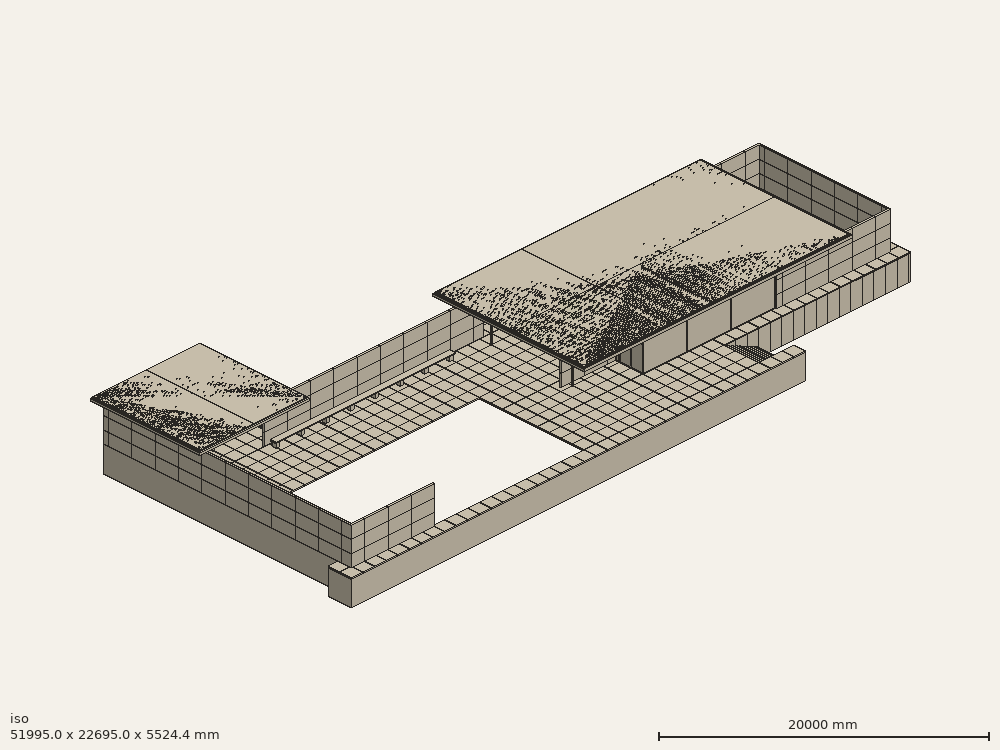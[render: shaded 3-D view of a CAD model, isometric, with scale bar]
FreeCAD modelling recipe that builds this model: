
FCSTD DOCUMENT  (FreeCAD 0.19R17174 (Git))
Label: Pabellon de Barcelona
License: All rights reserved
LicenseURL: http://en.wikipedia.org/wiki/All_rights_reserved
objects: Part::FeaturePython×94, Part::Part2DObjectPython×43, Part::Feature×31, App::DocumentObjectGroup×24, Sketcher::SketchObject×17, App::FeaturePython×11, Part::MultiCommon×6, Part::Fillet×2, TechDraw::DrawSVGTemplate×2, TechDraw::DrawPage×2, TechDraw::DrawViewDimension×2, Spreadsheet::Sheet×2, Part::Compound×1, Part::Offset2D×1, Surface::GeomFillSurface×1, Part::Cut×1, App::GeometryPython×1, TechDraw::DrawViewArch×1, TechDraw::DrawViewPart×1
note: 199 computed .brp shape members not serialized (recipe doc carries the construction recipe); baked Part::Feature solids carry a one-line shape summary decoded from their .brp

FEATURE [Part::Feature] Cancel
  Placement = pos=(-22160,-15160,0) rot=(0,0,1;0rad)
  shape: bbox 43800 x 17160 x 2e-07 mm, 0 faces, 0 solids (baked)
FEATURE [Part::Feature] Columns  label="Columns003"
  Placement = pos=(-22160,-15160,0) rot=(0,0,1;0rad)
  shape: bbox 19160 x 7160 x 2e-07 mm, 0 faces, 0 solids (baked)
FEATURE [Part::Feature] Crystal
  Placement = pos=(-22160,-15160,0) rot=(0,0,1;0rad)
  shape: bbox 43740 x 17150 x 2e-07 mm, 0 faces, 0 solids (baked)
FEATURE [Part::Feature] Doors  label="Doors003"
  Placement = pos=(-22160,-15160,0) rot=(0,0,1;0rad)
  shape: bbox 45870 x 16380 x 2e-07 mm, 0 faces, 0 solids (baked)
FEATURE [Part::Feature] Flooring  label="Flooring006"
  Placement = pos=(-22160,-15160,0) rot=(0,0,1;0rad)
  shape: bbox 52000 x 22000 x 2e-07 mm, 0 faces, 0 solids (baked)
FEATURE [Part::Feature] Furniture
  Placement = pos=(-22160,-15160,0) rot=(0,0,1;0rad)
  shape: bbox 43070 x 14280 x 2e-07 mm, 0 faces, 0 solids (baked)
FEATURE [Part::Feature] Projection
  Placement = pos=(-22160,-15160,0) rot=(0,0,1;0rad)
  shape: bbox 46650 x 18650 x 2e-07 mm, 0 faces, 0 solids (baked)
FEATURE [Part::Feature] Walls  label="Walls007"
  Placement = pos=(-22160,-15160,0) rot=(0,0,1;0rad)
  shape: bbox 50320 x 21420 x 2e-07 mm, 0 faces, 0 solids (baked)
FEATURE [App::DocumentObjectGroup] Group  label="Floor plan"
  Group = -> [Cancel,Columns,Crystal,Doors,Flooring,Furniture,Projection,Walls]
FEATURE [Part::Feature] Doors001
  Placement = pos=(-22160,-42510.2,3000) rot=(0,0,1;0rad)
  shape: bbox 618.1 x 595.2 x 2e-07 mm, 0 faces, 0 solids (baked)
FEATURE [Part::Feature] Flooring001
  Placement = pos=(-22160,-42510.2,3000) rot=(0,0,1;0rad)
  shape: bbox 52000 x 17000 x 2e-07 mm, 0 faces, 0 solids (baked)
FEATURE [Part::Feature] Furniture001
  Placement = pos=(-22160,-42510.2,3000) rot=(0,0,1;0rad)
  shape: bbox 13500 x 500 x 2e-07 mm, 0 faces, 0 solids (baked)
FEATURE [Part::Feature] Projection001
  Placement = pos=(-22160,-42510.2,3000) rot=(0,0,1;0rad)
  shape: bbox 1520 x 6220 x 2e-07 mm, 0 faces, 0 solids (baked)
FEATURE [Part::Feature] Roof
  Placement = pos=(-22160,-42510.2,3000) rot=(0,0,1;0rad)
  shape: bbox 46650 x 18650 x 2e-07 mm, 0 faces, 0 solids (baked)
FEATURE [Part::Feature] Walls001
  Placement = pos=(-22160,-42510.2,3000) rot=(0,0,1;0rad)
  shape: bbox 50320 x 15320 x 2e-07 mm, 0 faces, 0 solids (baked)
FEATURE [App::DocumentObjectGroup] Group001  label="Roof plan"
  Group = -> [Doors001,Flooring001,Furniture001,Projection001,Roof,Walls001]
FEATURE [Part::Feature] Cancel001
  Placement = pos=(-81287.8,-24500,-23959) rot=(1,0,0;1.5708rad)
  shape: bbox 11310 x 2e-07 x 2975 mm, 0 faces, 0 solids (baked)
FEATURE [Part::Feature] Columns001
  Placement = pos=(-81287.8,-24500,-23959) rot=(1,0,0;1.5708rad)
  shape: bbox 12830 x 2e-07 x 3000 mm, 0 faces, 0 solids (baked)
FEATURE [Part::Feature] Flooring002
  Placement = pos=(-81287.8,-24500,-23959) rot=(1,0,0;1.5708rad)
  shape: bbox 52000 x 2e-07 x 1600 mm, 0 faces, 0 solids (baked)
FEATURE [Part::Feature] Furniture002
  Placement = pos=(-81287.8,-24500,-23959) rot=(1,0,0;1.5708rad)
  shape: bbox 15200 x 2e-07 x 500 mm, 0 faces, 0 solids (baked)
FEATURE [Part::Feature] Roof001
  Placement = pos=(-81287.8,-24500,-23959) rot=(1,0,0;1.5708rad)
  shape: bbox 59640 x 2e-07 x 4974 mm, 0 faces, 0 solids (baked)
FEATURE [Part::Feature] Walls002
  Placement = pos=(-81287.8,-24500,-23959) rot=(1,0,0;1.5708rad)
  shape: bbox 50320 x 2e-07 x 3000 mm, 0 faces, 0 solids (baked)
FEATURE [App::DocumentObjectGroup] Group002  label="View front"
  Group = -> [Cancel001,Columns001,Flooring002,Furniture002,Roof001,Walls002]
FEATURE [Part::Feature] Cancel002
  Placement = pos=(89304.6,14800,-15495.3) rot=(0,0.707107,0.707107;3.14159rad)
  shape: bbox 32700 x 2e-07 x 3000 mm, 0 faces, 0 solids (baked)
FEATURE [Part::Feature] Columns002
  Placement = pos=(89304.6,14800,-15495.3) rot=(0,0.707107,0.707107;3.14159rad)
  shape: bbox 160 x 2e-07 x 3000 mm, 0 faces, 0 solids (baked)
FEATURE [Part::Feature] Roof002
  Placement = pos=(89304.6,14800,-15495.3) rot=(0,0.707107,0.707107;3.14159rad)
  shape: bbox 59640 x 2e-07 x 3836 mm, 0 faces, 0 solids (baked)
FEATURE [Part::Feature] Walls003
  Placement = pos=(89304.6,14800,-15495.3) rot=(0,0.707107,0.707107;3.14159rad)
  shape: bbox 50320 x 2e-07 x 3352 mm, 0 faces, 0 solids (baked)
FEATURE [App::DocumentObjectGroup] Group003  label="View back"
  Group = -> [Cancel002,Columns002,Roof002,Walls003]
FEATURE [Part::Feature] Flooring003
  Placement = pos=(-31600,63521.9,-6564.9) rot=(0.57735,-0.57735,-0.57735;2.0944rad)
  shape: bbox 2e-07 x 22160 x 3800 mm, 0 faces, 0 solids (baked)
FEATURE [Part::Feature] Roof003
  Placement = pos=(-31600,63521.9,-6564.9) rot=(0.57735,-0.57735,-0.57735;2.0944rad)
  shape: bbox 2e-07 x 18540 x 300 mm, 0 faces, 0 solids (baked)
FEATURE [Part::Feature] Walls004
  Placement = pos=(-31600,63521.9,-6564.9) rot=(0.57735,-0.57735,-0.57735;2.0944rad)
  shape: bbox 2e-07 x 26740 x 3800 mm, 0 faces, 0 solids (baked)
FEATURE [App::DocumentObjectGroup] Group004  label="View right"
  Group = -> [Flooring003,Roof003,Walls004]
FEATURE [Part::Feature] Cancel003
  Placement = pos=(39966.7,-107654,-7031.61) rot=(0.57735,0.57735,0.57735;2.0944rad)
  shape: bbox 2e-07 x 1800 x 400 mm, 0 faces, 0 solids (baked)
FEATURE [Part::Feature] Flooring004
  Placement = pos=(39966.7,-107654,-7031.61) rot=(0.57735,0.57735,0.57735;2.0944rad)
  shape: bbox 2e-07 x 6000 x 1267 mm, 0 faces, 0 solids (baked)
FEATURE [Part::Feature] Roof004
  Placement = pos=(39966.7,-107654,-7031.61) rot=(0.57735,0.57735,0.57735;2.0944rad)
  shape: bbox 2e-07 x 24790 x 4567 mm, 0 faces, 0 solids (baked)
FEATURE [Part::Feature] Walls005
  Placement = pos=(39966.7,-107654,-7031.61) rot=(0.57735,0.57735,0.57735;2.0944rad)
  shape: bbox 2e-07 x 22620 x 4267 mm, 0 faces, 0 solids (baked)
FEATURE [App::DocumentObjectGroup] Group005  label="View left"
  Group = -> [Cancel003,Flooring004,Roof004,Walls005]
FEATURE [Part::Part2DObjectPython] Wire  # Draft 2D object (typed FeaturePython)
  ChamferSize = 0
  Closed = false
  End = (-13840,840,0)
  FilletRadius = 0
  Length = 42120
  MakeFace = true
  Placement = pos=(-15000,-15160,0) rot=(0,0,1;0rad)
  Points = (5) [(0,0,0),(-7160,0,0),(-7160,21320,0),(1160,21320,0),(1160,16000,0)]
  Start = (-15000,-15160,0)
  Subdivisions = 0
FEATURE [Part::Part2DObjectPython] Line  # Draft 2D object (typed FeaturePython)
  ChamferSize = 0
  Closed = false
  End = (3330,-840,0)
  FilletRadius = 0
  Length = 18830
  MakeFace = true
  Placement = pos=(-15500,-840,0) rot=(0,0,1;0rad)
  Points = (2) [(0,0,0),(18830,0,0)]
  Start = (-15500,-840,0)
  Subdivisions = 0
FEATURE [Part::Part2DObjectPython] Wire001  # Draft 2D object (typed FeaturePython)
  ChamferSize = 0
  Closed = false
  End = (18333.3,-11160,0)
  FilletRadius = 0
  Length = 34506.7
  MakeFace = true
  Placement = pos=(14800,160,0) rot=(0,0,1;0rad)
  Points = (4) [(0,0,0),(13360,0,0),(13360,-11320,0),(3533.33,-11320,0)]
  Start = (14800,160,0)
  Subdivisions = 0
FEATURE [Part::Part2DObjectPython] Line001  # Draft 2D object (typed FeaturePython)
  ChamferSize = 0
  Closed = false
  End = (9666.67,-8670,0)
  FilletRadius = 0
  Length = 7333.33
  MakeFace = true
  Placement = pos=(2333.33,-8670,0) rot=(0,0,1;0rad)
  Points = (2) [(0,0,0),(7333.33,0,0)]
  Start = (2333.33,-8670,0)
  Subdivisions = 0
FEATURE [Part::Part2DObjectPython] Line002  # Draft 2D object (typed FeaturePython)
  ChamferSize = 0
  Closed = false
  End = (19330,-4510,0)
  FilletRadius = 0
  Length = 5160
  MakeFace = true
  Placement = pos=(14170,-4510,0) rot=(0,0,1;0rad)
  Points = (2) [(0,0,0),(5160,0,0)]
  Start = (14170,-4510,0)
  Subdivisions = 0
FEATURE [Part::Part2DObjectPython] Line003  # Draft 2D object (typed FeaturePython)
  ChamferSize = 0
  Closed = false
  End = (-18050,6000,0)
  FilletRadius = 0
  Length = 5160
  MakeFace = true
  Placement = pos=(-18050,840,0) rot=(0,0,1;0rad)
  Points = (2) [(0,0,0),(-8.73115e-11,5160,0)]
  Start = (-18050,840,0)
  Subdivisions = 0
FEATURE [Part::Part2DObjectPython] Line004  # Draft 2D object (typed FeaturePython)
  ChamferSize = 0
  Closed = false
  End = (-14000,4500,0)
  FilletRadius = 0
  Length = 3950
  MakeFace = true
  Placement = pos=(-17950,4500,0) rot=(0,0,1;0rad)
  Points = (2) [(0,0,0),(3950,0,0)]
  Start = (-17950,4500,0)
  Subdivisions = 0
FEATURE [Part::Part2DObjectPython] Line005  # Draft 2D object (typed FeaturePython)
  ChamferSize = 0
  Closed = false
  End = (-16050,4600,0)
  FilletRadius = 0
  Length = 1400
  MakeFace = true
  Placement = pos=(-16050,6000,0) rot=(0,0,1;0rad)
  Points = (2) [(0,0,0),(0,-1400,0)]
  Start = (-16050,6000,0)
  Subdivisions = 0
FEATURE [Part::FeaturePython] Wall  # Arch/BIM 150 (typed FeaturePython)
  Align = 0
  Base = -> Wire
  BlockHeight = 1000
  BlockLength = 2000
  CountBroken = 15
  CountEntire = 52
  Face = 0
  Height = 3000
  HorizontalArea = 7.3024e+06
  IfcData = IfcUID=0OLEO4RqaHwRzx093rt3ko,+1 more (map truncated)
  IfcType = 150
  Joint = 0
  Length = 42120
  MakeBlocks = true
  MoveBase = false
  MoveWithHost = true
  Normal = (0,0,0)
  OffsetFirst = 0
  OffsetSecond = 0
  PerimeterLength = 83600
  PredefinedType = 0
  VerticalArea = 2.46192e+08
  Width = 160
FEATURE [Part::FeaturePython] Wall001  # Arch/BIM 150 (typed FeaturePython)
  Align = 0
  Base = -> Line
  BlockHeight = 1000
  BlockLength = 2000
  CountBroken = 3
  CountEntire = 27
  Face = 0
  Height = 3000
  HorizontalArea = 3.0128e+06
  IfcData = IfcUID=0OKnYcRqaHwRzx093rt3ko,+1 more (map truncated)
  IfcType = 150
  Joint = 0
  Length = 18830
  MakeBlocks = true
  MoveBase = false
  MoveWithHost = true
  Normal = (0,0,0)
  OffsetFirst = 0
  OffsetSecond = 0
  PerimeterLength = 37980
  PredefinedType = 0
  VerticalArea = 1.1394e+08
  Width = 160
FEATURE [Part::FeaturePython] Wall002  # Arch/BIM 150 (typed FeaturePython)
  Align = 0
  Base = -> Wire001
  BlockHeight = 1000
  BlockLength = 2000
  CountBroken = 9
  CountEntire = 45
  Face = 0
  Height = 3000
  HorizontalArea = 5.46987e+06
  IfcData = IfcUID=0ONTaSRqaHwRzx093rt3ko,+1 more (map truncated)
  IfcType = 150
  Joint = 0
  Length = 34506.7
  MakeBlocks = true
  MoveBase = false
  MoveWithHost = true
  Normal = (0,0,0)
  OffsetFirst = 0
  OffsetSecond = 0
  PerimeterLength = 68693.3
  PredefinedType = 0
  VerticalArea = 2.0608e+08
  Width = 160
FEATURE [Part::FeaturePython] Wall003  # Arch/BIM 150 (typed FeaturePython)
  Align = 1
  Base = -> Line001
  BlockHeight = 1000
  BlockLength = 2000
  CountBroken = 3
  CountEntire = 9
  Face = 0
  Height = 3000
  HorizontalArea = 1.17333e+06
  IfcData = IfcUID=0OO35ERqaHwRzx093rt3ko,+1 more (map truncated)
  IfcType = 150
  Joint = 0
  Length = 7333.33
  MakeBlocks = true
  MoveBase = false
  MoveWithHost = true
  Normal = (0,0,0)
  OffsetFirst = 0
  OffsetSecond = 0
  PerimeterLength = 14986.7
  PredefinedType = 0
  VerticalArea = 4.496e+07
  Width = 160
FEATURE [Part::FeaturePython] Wall004  # Arch/BIM 150 (typed FeaturePython)
  Align = 0
  Base = -> Line002
  BlockHeight = 0
  BlockLength = 0
  CountBroken = 0
  CountEntire = 0
  Face = 0
  Height = 3000
  HorizontalArea = 825600
  IfcData = IfcUID=0OORcIRqaHwRzx093rt3ko,+1 more (map truncated)
  IfcType = 150
  Joint = 0
  Length = 5160
  MakeBlocks = false
  MoveBase = false
  MoveWithHost = true
  Normal = (0,0,0)
  OffsetFirst = 0
  OffsetSecond = 0
  PerimeterLength = 10640
  PredefinedType = 0
  VerticalArea = 3.192e+07
  Width = 160
FEATURE [Part::FeaturePython] Wall005  # Arch/BIM 150 (typed FeaturePython)
  Align = 0
  Base = -> Line003
  BlockHeight = 0
  BlockLength = 0
  CountBroken = 0
  CountEntire = 0
  Face = 0
  Height = 3000
  HorizontalArea = 516000
  IfcData = IfcUID=0OOnwaRqaHwRzx093rt3ko,+1 more (map truncated)
  IfcType = 150
  Joint = 0
  Length = 5160
  MakeBlocks = false
  MoveBase = false
  MoveWithHost = true
  Normal = (0,0,0)
  OffsetFirst = 0
  OffsetSecond = 0
  PerimeterLength = 10520
  PredefinedType = 0
  VerticalArea = 2.778e+07
  Width = 100
FEATURE [Part::FeaturePython] Wall006  # Arch/BIM 150 (typed FeaturePython)
  Align = 1
  Base = -> Line004
  BlockHeight = 0
  BlockLength = 0
  CountBroken = 0
  CountEntire = 0
  Face = 0
  Height = 3000
  HorizontalArea = 395000
  IfcData = IfcUID=0OQ8YARqaHwRzx093rt3ko,+1 more (map truncated)
  IfcType = 150
  Joint = 0
  Length = 3950
  MakeBlocks = false
  MoveBase = false
  MoveWithHost = true
  Normal = (0,0,0)
  OffsetFirst = 0
  OffsetSecond = 0
  PerimeterLength = 8100
  PredefinedType = 0
  VerticalArea = 2.136e+07
  Width = 100
FEATURE [Part::FeaturePython] Wall007  # Arch/BIM 150 (typed FeaturePython)
  Align = 1
  Base = -> Line005
  BlockHeight = 0
  BlockLength = 0
  CountBroken = 0
  CountEntire = 0
  Face = 0
  Height = 3000
  HorizontalArea = 140000
  IfcData = IfcUID=0ORbNGRqaHwRzx093rt3ko,+1 more (map truncated)
  IfcType = 150
  Joint = 0
  Length = 1400
  MakeBlocks = false
  MoveBase = false
  MoveWithHost = true
  Normal = (0,0,0)
  OffsetFirst = 0
  OffsetSecond = 0
  PerimeterLength = 3000
  PredefinedType = 0
  VerticalArea = 5640000
  Width = 100
FEATURE [Part::Part2DObjectPython] Rectangle  # Draft 2D object (typed FeaturePython)
  ChamferSize = 0
  Columns = 1
  FilletRadius = 0
  Height = 600
  Length = 4000
  MakeFace = false
  Placement = pos=(-14000,6160,2000) rot=(0,0.707107,0.707107;3.14159rad)
  Rows = 1
  Support = -> [Wall]
FEATURE [Part::Part2DObjectPython] Rectangle001  # Draft 2D object (typed FeaturePython)
  ChamferSize = 0
  Columns = 1
  FilletRadius = 0
  Height = 400
  Length = 1850
  MakeFace = false
  Placement = pos=(-14100,6160,2100) rot=(0,0.707107,0.707107;3.14159rad)
  Rows = 1
FEATURE [Part::Part2DObjectPython] Rectangle002  # Draft 2D object (typed FeaturePython)
  ChamferSize = 0
  Columns = 1
  FilletRadius = 0
  Height = 400
  Length = 1850
  MakeFace = false
  Placement = pos=(-16050,6160,2100) rot=(0,0.707107,0.707107;3.14159rad)
  Rows = 1
FEATURE [Part::Compound] Compound
  Links = -> [Rectangle,Rectangle001,Rectangle002]
FEATURE [Part::FeaturePython] Window  # Arch/BIM 154 (typed FeaturePython)
  Area = 0
  Base = -> Compound
  Frame = 0
  Height = 0
  HoleDepth = 0
  HoleWire = 0
  HorizontalArea = 0
  Hosts = -> [Wall]
  IfcData = IfcUID=0OMAYERqaHwRzx093rt3ko,+1 more (map truncated)
  IfcType = 154
  LouvreSpacing = 0
  LouvreWidth = 0
  MoveBase = false
  MoveWithHost = true
  Normal = (0,-1,0)
  Offset = 55
  Opening = 0
  OverallHeight = 0
  OverallWidth = 0
  PartitioningType = 0
  PerimeterLength = 0
  PredefinedType = 0
  Preset = 0
  SymbolElevation = false
  SymbolPlan = false
  VerticalArea = 0
  Width = 0
  WindowParts = Window frame | Frame | Wire0,Wire1,Wire2 | 50.0 | 0.0+V | Glass 1 | Glass panel | Wire1 | 10.0 | 20.0+V | Glass 2 | Glass panel | Wire2 | 10.0 | 20.0+V
  expr: OverallWidth = Width.Value
  expr: OverallHeight = Height.Value
FEATURE [Sketcher::SketchObject] Sketch
  Placement = pos=(-17150,4500,0) rot=(1,0,0;1.5708rad)
  sketch-geometry (8):
    g0: LineSegment StartX=0 StartY=0 StartZ=0 EndX=800 EndY=0 EndZ=0
    g1: LineSegment StartX=800 StartY=0 StartZ=0 EndX=800 EndY=2100 EndZ=0
    g2: LineSegment StartX=800 StartY=2100 StartZ=0 EndX=0 EndY=2100 EndZ=0
    g3: LineSegment StartX=0 StartY=2100 StartZ=0 EndX=0 EndY=0 EndZ=0
    g4: LineSegment StartX=30 StartY=0 StartZ=0 EndX=770 EndY=0 EndZ=0
    g5: LineSegment StartX=770 StartY=0 StartZ=0 EndX=770 EndY=2070 EndZ=0
    g6: LineSegment StartX=770 StartY=2070 StartZ=0 EndX=30 EndY=2070 EndZ=0
    g7: LineSegment StartX=30 StartY=2070 StartZ=0 EndX=30 EndY=0 EndZ=0
  constraints (23):
    c: Coincident(g0,g1)
    c: Coincident(g1,g2)
    c: Coincident(g2,g3)
    c: Coincident(g3,g0)
    c: Horizontal(g0)
    c: Horizontal(g2)
    c: Vertical(g1)
    c: Vertical(g3)
    c: Coincident(g4,g5)
    c: Coincident(g5,g6)
    c: Coincident(g6,g7)
    c: Coincident(g7,g4)
    c: Horizontal(g4)
    c: Horizontal(g6)
    c: Vertical(g5)
    c: Vertical(g7)
    c: DistanceY(g1) = 2100  'Height'
    c: DistanceX(g0) = 800  'Width'
    c: DistanceY(g6,g2) = 30  'Frame1'
    c: DistanceX(g2,g6) = 30  'Frame2'
    c: DistanceX(g4,g0) = 30  'Frame3'
    c: DistanceY(g0,g4) = 0
    c: Coincident(g0,g-1)
FEATURE [Part::FeaturePython] Window001  label="Wooden door 80x210 001"  # Arch/BIM 41 (typed FeaturePython)
  Area = 1680000
  Base = -> Sketch
  Frame = 30
  Height = 2100
  HoleDepth = 0
  HoleWire = 0
  HorizontalArea = 0
  Hosts = -> [Wall006]
  IfcData = IfcUID=0OQpl0RqaHwRzx093rt3ko,+1 more (map truncated)
  IfcType = 41
  LouvreSpacing = 0
  LouvreWidth = 0
  MoveBase = false
  MoveWithHost = true
  Normal = (0,1,-2e-16)
  Opening = 0
  OperationType = 0
  OverallHeight = 2100
  OverallWidth = 800
  PerimeterLength = 0
  PredefinedType = 0
  Preset = 6
  SymbolElevation = false
  SymbolPlan = false
  VerticalArea = 0
  Width = 800
  WindowParts = OuterFrame | Frame | Wire0,Wire1 | 30.0+V | 0.00+V | Door | Solid panel | Wire1 | 30.0 | 30.0+V
  expr: OverallWidth = Width.Value
  expr: OverallHeight = Height.Value
FEATURE [Sketcher::SketchObject] Sketch001
  Placement = pos=(-16050,5400,0) rot=(0.57735,-0.57735,-0.57735;2.0944rad)
  sketch-geometry (8):
    g0: LineSegment StartX=0 StartY=0 StartZ=0 EndX=800 EndY=0 EndZ=0
    g1: LineSegment StartX=800 StartY=0 StartZ=0 EndX=800 EndY=2100 EndZ=0
    g2: LineSegment StartX=800 StartY=2100 StartZ=0 EndX=0 EndY=2100 EndZ=0
    g3: LineSegment StartX=0 StartY=2100 StartZ=0 EndX=0 EndY=0 EndZ=0
    g4: LineSegment StartX=30 StartY=0 StartZ=0 EndX=770 EndY=0 EndZ=0
    g5: LineSegment StartX=770 StartY=0 StartZ=0 EndX=770 EndY=2070 EndZ=0
    g6: LineSegment StartX=770 StartY=2070 StartZ=0 EndX=30 EndY=2070 EndZ=0
    g7: LineSegment StartX=30 StartY=2070 StartZ=0 EndX=30 EndY=0 EndZ=0
  constraints (23):
    c: Coincident(g0,g1)
    c: Coincident(g1,g2)
    c: Coincident(g2,g3)
    c: Coincident(g3,g0)
    c: Horizontal(g0)
    c: Horizontal(g2)
    c: Vertical(g1)
    c: Vertical(g3)
    c: Coincident(g4,g5)
    c: Coincident(g5,g6)
    c: Coincident(g6,g7)
    c: Coincident(g7,g4)
    c: Horizontal(g4)
    c: Horizontal(g6)
    c: Vertical(g5)
    c: Vertical(g7)
    c: DistanceY(g1) = 2100  'Height'
    c: DistanceX(g0) = 800  'Width'
    c: DistanceY(g6,g2) = 30  'Frame1'
    c: DistanceX(g2,g6) = 30  'Frame2'
    c: DistanceX(g4,g0) = 30  'Frame3'
    c: DistanceY(g0,g4) = 0
    c: Coincident(g0,g-1)
FEATURE [Part::FeaturePython] Window002  label="Wooden door 80x210 "  # Arch/BIM 41 (typed FeaturePython)
  Area = 1680000
  Base = -> Sketch001
  Frame = 30
  Height = 2100
  HoleDepth = 0
  HoleWire = 0
  HorizontalArea = 0
  Hosts = -> [Wall007]
  IfcData = IfcUID=0OSF62RqaHwRzx093rt3ko,+1 more (map truncated)
  IfcType = 41
  LouvreSpacing = 0
  LouvreWidth = 0
  MoveBase = false
  MoveWithHost = true
  Normal = (1,0,0)
  Opening = 0
  OperationType = 0
  OverallHeight = 2100
  OverallWidth = 800
  PerimeterLength = 0
  PredefinedType = 0
  Preset = 6
  SymbolElevation = false
  SymbolPlan = false
  VerticalArea = 0
  Width = 800
  WindowParts = OuterFrame | Frame | Wire0,Wire1 | 30.0+V | 0.00+V | Door | Solid panel | Wire1 | 30.0 | 30.0+V
  expr: OverallWidth = Width.Value
  expr: OverallHeight = Height.Value
FEATURE [Sketcher::SketchObject] Sketch002
  Placement = pos=(-17950,3000,0) rot=(0.57735,0.57735,0.57735;2.0944rad)
  sketch-geometry (8):
    g0: LineSegment StartX=0 StartY=0 StartZ=0 EndX=1000 EndY=0 EndZ=0
    g1: LineSegment StartX=1000 StartY=0 StartZ=0 EndX=1000 EndY=2100 EndZ=0
    g2: LineSegment StartX=1000 StartY=2100 StartZ=0 EndX=0 EndY=2100 EndZ=0
    g3: LineSegment StartX=0 StartY=2100 StartZ=0 EndX=0 EndY=0 EndZ=0
    g4: LineSegment StartX=30 StartY=0 StartZ=0 EndX=970 EndY=0 EndZ=0
    g5: LineSegment StartX=970 StartY=0 StartZ=0 EndX=970 EndY=2070 EndZ=0
    g6: LineSegment StartX=970 StartY=2070 StartZ=0 EndX=30 EndY=2070 EndZ=0
    g7: LineSegment StartX=30 StartY=2070 StartZ=0 EndX=30 EndY=0 EndZ=0
  constraints (23):
    c: Coincident(g0,g1)
    c: Coincident(g1,g2)
    c: Coincident(g2,g3)
    c: Coincident(g3,g0)
    c: Horizontal(g0)
    c: Horizontal(g2)
    c: Vertical(g1)
    c: Vertical(g3)
    c: Coincident(g4,g5)
    c: Coincident(g5,g6)
    c: Coincident(g6,g7)
    c: Coincident(g7,g4)
    c: Horizontal(g4)
    c: Horizontal(g6)
    c: Vertical(g5)
    c: Vertical(g7)
    c: DistanceY(g1) = 2100  'Height'
    c: DistanceX(g0) = 1000  'Width'
    c: DistanceY(g6,g2) = 30  'Frame1'
    c: DistanceX(g2,g6) = 30  'Frame2'
    c: DistanceX(g4,g0) = 30  'Frame3'
    c: DistanceY(g0,g4) = 0
    c: Coincident(g0,g-1)
FEATURE [Part::FeaturePython] Window003  label="Wooden door 100x210"  # Arch/BIM 41 (typed FeaturePython)
  Area = 2100000
  Base = -> Sketch002
  Frame = 30
  Height = 2100
  HoleDepth = 0
  HoleWire = 0
  HorizontalArea = 0
  Hosts = -> [Wall005]
  IfcData = IfcUID=0OPMYARqaHwRzx093rt3ko,+1 more (map truncated)
  IfcType = 41
  LouvreSpacing = 0
  LouvreWidth = 0
  MoveBase = false
  MoveWithHost = true
  Normal = (-1,-8.4e-15,8.4e-15)
  Opening = 0
  OperationType = 0
  OverallHeight = 2100
  OverallWidth = 1000
  PerimeterLength = 0
  PredefinedType = 0
  Preset = 6
  SymbolElevation = false
  SymbolPlan = false
  VerticalArea = 0
  Width = 1000
  WindowParts = OuterFrame | Frame | Wire0,Wire1 | 30.0+V | 0.00+V | Door | Solid panel | Wire1 | 30.0 | 30.0+V
  expr: OverallWidth = Width.Value
  expr: OverallHeight = Height.Value
FEATURE [Sketcher::SketchObject] Sketch003
  Placement = pos=(4800,-11100,0) rot=(1,0,0;1.5708rad)
  sketch-geometry (24):
    g0: LineSegment StartX=0 StartY=0 StartZ=0 EndX=2000 EndY=0 EndZ=0
    g1: LineSegment StartX=2000 StartY=0 StartZ=0 EndX=2000 EndY=2100 EndZ=0
    g2: LineSegment StartX=2000 StartY=2100 StartZ=0 EndX=0 EndY=2100 EndZ=0
    g3: LineSegment StartX=0 StartY=2100 StartZ=0 EndX=0 EndY=0 EndZ=0
    g4: LineSegment StartX=30 StartY=1.7147 StartZ=0 EndX=1970 EndY=1.7147 EndZ=0
    g5: LineSegment StartX=1970 StartY=1.7147 StartZ=0 EndX=1970 EndY=2070 EndZ=0
    g6: LineSegment StartX=1970 StartY=2070 StartZ=0 EndX=30 EndY=2070 EndZ=0
    g7: LineSegment StartX=30 StartY=2070 StartZ=0 EndX=30 EndY=1.7147 EndZ=0
    g8: LineSegment StartX=33 StartY=4.7147 StartZ=0 EndX=998.5 EndY=4.7147 EndZ=0
    g9: LineSegment StartX=998.5 StartY=4.7147 StartZ=0 EndX=998.5 EndY=2067 EndZ=0
    g10: LineSegment StartX=998.5 StartY=2067 StartZ=0 EndX=33 EndY=2067 EndZ=0
    g11: LineSegment StartX=33 StartY=2067 StartZ=0 EndX=33 EndY=4.7147 EndZ=0
    g12: LineSegment StartX=63 StartY=34.7147 StartZ=0 EndX=968.5 EndY=34.7147 EndZ=0
    g13: LineSegment StartX=968.5 StartY=34.7147 StartZ=0 EndX=968.5 EndY=2037 EndZ=0
    g14: LineSegment StartX=968.5 StartY=2037 StartZ=0 EndX=63 EndY=2037 EndZ=0
    g15: LineSegment StartX=63 StartY=2037 StartZ=0 EndX=63 EndY=34.7147 EndZ=0
    g16: LineSegment StartX=1001.5 StartY=4.7147 StartZ=0 EndX=1967 EndY=4.7147 EndZ=0
    g17: LineSegment StartX=1967 StartY=4.7147 StartZ=0 EndX=1967 EndY=2067 EndZ=0
    g18: LineSegment StartX=1967 StartY=2067 StartZ=0 EndX=1001.5 EndY=2067 EndZ=0
    g19: LineSegment StartX=1001.5 StartY=2067 StartZ=0 EndX=1001.5 EndY=4.7147 EndZ=0
    g20: LineSegment StartX=1031.5 StartY=34.7147 StartZ=0 EndX=1937 EndY=34.7147 EndZ=0
    g21: LineSegment StartX=1937 StartY=34.7147 StartZ=0 EndX=1937 EndY=2037 EndZ=0
    g22: LineSegment StartX=1937 StartY=2037 StartZ=0 EndX=1031.5 EndY=2037 EndZ=0
    g23: LineSegment StartX=1031.5 StartY=2037 StartZ=0 EndX=1031.5 EndY=34.7147 EndZ=0
  constraints (70):
    c: Coincident(g0,g1)
    c: Coincident(g1,g2)
    c: Coincident(g2,g3)
    c: Coincident(g3,g0)
    c: Horizontal(g0)
    c: Horizontal(g2)
    c: Vertical(g1)
    c: Vertical(g3)
    c: Coincident(g4,g5)
    c: Coincident(g5,g6)
    c: Coincident(g6,g7)
    c: Coincident(g7,g4)
    c: Horizontal(g4)
    c: Horizontal(g6)
    c: Vertical(g5)
    c: Vertical(g7)
    c: DistanceY(g1) = 2100  'Height'
    c: DistanceX(g0) = 2000  'Width'
    c: DistanceY(g6,g2) = 30  'Frame1'
    c: DistanceX(g2,g6) = 30  'Frame2'
    c: DistanceX(g4,g0) = 30  'Frame3'
    c: Coincident(g0,g-1)
    c: Coincident(g8,g9)
    c: Coincident(g9,g10)
    c: Coincident(g10,g11)
    c: Coincident(g11,g8)
    c: Horizontal(g8)
    c: Horizontal(g10)
    c: Vertical(g9)
    c: Vertical(g11)
    c: Coincident(g12,g13)
    c: Coincident(g13,g14)
    c: Coincident(g14,g15)
    c: Coincident(g15,g12)
    c: Horizontal(g12)
    c: Horizontal(g14)
    c: Vertical(g13)
    c: Vertical(g15)
    c: Coincident(g16,g17)
    c: Coincident(g17,g18)
    c: Coincident(g18,g19)
    c: Coincident(g19,g16)
    c: Horizontal(g16)
    c: Horizontal(g18)
    c: Vertical(g17)
    c: Vertical(g19)
    c: Coincident(g20,g21)
    c: Coincident(g21,g22)
    c: Coincident(g22,g23)
    c: Coincident(g23,g20)
    c: Horizontal(g20)
    c: Horizontal(g22)
    c: Vertical(g21)
    c: Vertical(g23)
    c: DistanceY(g8,g12) = 30  'Frame5'
    c: DistanceX(g8,g12) = 30  'Frame6'
    c: DistanceX(g21,g17) = 30  'Frame7'
    c: DistanceY(g21,g17) = 30  'Frame8'
    c: DistanceX(g16,g20) = 30  'Frame9'
    c: DistanceX(g14,g10) = 30  'Frame10'
    c: Equal(g22,g14)
    c: DistanceY(g8,g16) = 0
    c: DistanceY(g10,g18) = 0
    c: DistanceX(g4,g8) = 3
    c: DistanceY(g4,g8) = 3
    c: DistanceX(g6,g18) = -3
    c: DistanceY(g6,g18) = -3
    c: DistanceX(g9,g19) = 3
    c: PointOnObject(g13,g22)
    c: PointOnObject(g20,g12)
FEATURE [Part::FeaturePython] Window004  label="Glass door double 200x210 "  # Arch/BIM 41 (typed FeaturePython)
  Area = 4200000
  Base = -> Sketch003
  Frame = 30
  Height = 2100
  HoleDepth = 0
  HoleWire = 0
  HorizontalArea = 0
  IfcData = IfcUID=0OgMsCRqaHwRzx093rt3ko,+1 more (map truncated)
  IfcType = 41
  LouvreSpacing = 0
  LouvreWidth = 0
  MoveBase = false
  MoveWithHost = true
  Normal = (0,1,-2e-16)
  Opening = 0
  OperationType = 0
  OverallHeight = 2100
  OverallWidth = 2000
  PerimeterLength = 0
  Placement = pos=(18100,-4200,0) rot=(0,0,-1;1.5708rad)
  PredefinedType = 0
  Preset = 3
  SymbolElevation = false
  SymbolPlan = false
  VerticalArea = 0
  Width = 2000
  WindowParts = OuterFrame | Frame | Wire0,Wire1 | 30.0+V | 0.00+V | LeftFrame | Frame | Wire2,Wire3 | 30.0 | 30.0+V | LeftGlass | Glass panel | Wire3 | 3.0 | 45.0+V | RightFrame | Frame | Wire4,Wire5 | 30.0 | 30.0+V | RightGlass | Glass panel | Wire5 | 3.0 | 45.0+V
  expr: OverallWidth = Width.Value
  expr: OverallHeight = Height.Value
FEATURE [Part::FeaturePython] Window005  label="Glass door double 200x210 001"  # Arch/BIM 41 (typed FeaturePython)
  Area = 4200000
  CloneOf = -> Window004
  Frame = 0
  Height = 2100
  HoleDepth = 0
  HoleWire = 0
  HorizontalArea = 0
  IfcData = IfcUID=0OiBIsRqaHwRzx093rt3ko,+1 more (map truncated)
  IfcType = 41
  LouvreSpacing = 0
  LouvreWidth = 0
  MoveBase = false
  MoveWithHost = true
  Normal = (0,0,0)
  Opening = 0
  OperationType = 0
  OverallHeight = 2100
  OverallWidth = 2000
  PerimeterLength = 0
  Placement = pos=(27070,4800,0) rot=(0,0,-1;1.5708rad)
  PredefinedType = 0
  Preset = 0
  SymbolElevation = false
  SymbolPlan = false
  VerticalArea = 0
  Width = 2000
  expr: OverallWidth = Width.Value
  expr: OverallHeight = Height.Value
FEATURE [Sketcher::SketchObject] Sketch004
  Placement = pos=(-15975,974.662,0) rot=(1,0,0;1.5708rad)
  sketch-geometry (16):
    g0: LineSegment StartX=0 StartY=0 StartZ=0 EndX=950 EndY=0 EndZ=0
    g1: LineSegment StartX=950 StartY=0 StartZ=0 EndX=950 EndY=2100 EndZ=0
    g2: LineSegment StartX=950 StartY=2100 StartZ=0 EndX=0 EndY=2100 EndZ=0
    g3: LineSegment StartX=0 StartY=2100 StartZ=0 EndX=0 EndY=0 EndZ=0
    g4: LineSegment StartX=30 StartY=0 StartZ=0 EndX=920 EndY=0 EndZ=0
    g5: LineSegment StartX=920 StartY=0 StartZ=0 EndX=920 EndY=2070 EndZ=0
    g6: LineSegment StartX=920 StartY=2070 StartZ=0 EndX=30 EndY=2070 EndZ=0
    g7: LineSegment StartX=30 StartY=2070 StartZ=0 EndX=30 EndY=0 EndZ=0
    g8: LineSegment StartX=33 StartY=3 StartZ=0 EndX=917 EndY=3 EndZ=0
    g9: LineSegment StartX=917 StartY=3 StartZ=0 EndX=917 EndY=2067 EndZ=0
    g10: LineSegment StartX=917 StartY=2067 StartZ=0 EndX=33 EndY=2067 EndZ=0
    g11: LineSegment StartX=33 StartY=2067 StartZ=0 EndX=33 EndY=3 EndZ=0
    g12: LineSegment StartX=63 StartY=33 StartZ=0 EndX=887 EndY=33 EndZ=0
    g13: LineSegment StartX=887 StartY=33 StartZ=0 EndX=887 EndY=2037 EndZ=0
    g14: LineSegment StartX=887 StartY=2037 StartZ=0 EndX=63 EndY=2037 EndZ=0
    g15: LineSegment StartX=63 StartY=2037 StartZ=0 EndX=63 EndY=33 EndZ=0
  constraints (47):
    c: Coincident(g0,g1)
    c: Coincident(g1,g2)
    c: Coincident(g2,g3)
    c: Coincident(g3,g0)
    c: Horizontal(g0)
    c: Horizontal(g2)
    c: Vertical(g1)
    c: Vertical(g3)
    c: Coincident(g4,g5)
    c: Coincident(g5,g6)
    c: Coincident(g6,g7)
    c: Coincident(g7,g4)
    c: Horizontal(g4)
    c: Horizontal(g6)
    c: Vertical(g5)
    c: Vertical(g7)
    c: DistanceY(g1) = 2100  'Height'
    c: DistanceX(g0) = 950  'Width'
    c: DistanceY(g6,g2) = 30  'Frame1'
    c: DistanceX(g2,g6) = 30  'Frame2'
    c: DistanceX(g4,g0) = 30  'Frame3'
    c: DistanceY(g0,g4) = 0
    c: Coincident(g0,g-1)
    c: Coincident(g8,g9)
    c: Coincident(g9,g10)
    c: Coincident(g10,g11)
    c: Coincident(g11,g8)
    c: Horizontal(g8)
    c: Horizontal(g10)
    c: Vertical(g9)
    c: Vertical(g11)
    c: Coincident(g12,g13)
    c: Coincident(g13,g14)
    c: Coincident(g14,g15)
    c: Coincident(g15,g12)
    c: Horizontal(g12)
    c: Horizontal(g14)
    c: Vertical(g13)
    c: Vertical(g15)
    c: DistanceX(g8,g12) = 30  'Frame5'
    c: DistanceY(g8,g12) = 30  'Frame6'
    c: DistanceX(g14,g10) = 30  'Frame8'
    c: DistanceY(g14,g10) = 30  'Frame7'
    c: DistanceX(g4,g8) = 3
    c: DistanceY(g4,g8) = 3
    c: DistanceX(g10,g6) = 3
    c: DistanceY(g10,g6) = 3
FEATURE [Part::FeaturePython] Window006  label="Glass door simple 95x210"  # Arch/BIM 41 (typed FeaturePython)
  Area = 1995000
  Base = -> Sketch004
  Frame = 30
  Height = 2100
  HoleDepth = 0
  HoleWire = 0
  HorizontalArea = 0
  IfcData = IfcUID=0OiKJuRqaHwRzx093rt3ko,+1 more (map truncated)
  IfcType = 41
  LouvreSpacing = 0
  LouvreWidth = 0
  MoveBase = false
  MoveWithHost = true
  Normal = (0,1,-2e-16)
  Opening = 0
  OperationType = 0
  OverallHeight = 2100
  OverallWidth = 950
  PerimeterLength = 0
  PredefinedType = 0
  Preset = 7
  SymbolElevation = false
  SymbolPlan = false
  VerticalArea = 0
  Width = 950
  WindowParts = OuterFrame | Frame | Wire0,Wire1 | 30.0+V | 0.00+V | InnerFrame | Frame | Wire2,Wire3 | 30.0 | 30.0+V | InnerGlass | Glass panel | Wire3 | 3.0 | 45.0+V
  expr: OverallWidth = Width.Value
  expr: OverallHeight = Height.Value
FEATURE [Sketcher::SketchObject] Sketch005
  Placement = pos=(-20400,-1800,0) rot=(0.57735,0.57735,0.57735;2.0944rad)
  sketch-geometry (8):
    g0: LineSegment StartX=0 StartY=0 StartZ=0 EndX=2000 EndY=0 EndZ=0
    g1: LineSegment StartX=2000 StartY=0 StartZ=0 EndX=2000 EndY=3000 EndZ=0
    g2: LineSegment StartX=2000 StartY=3000 StartZ=0 EndX=0 EndY=3000 EndZ=0
    g3: LineSegment StartX=0 StartY=3000 StartZ=0 EndX=0 EndY=0 EndZ=0
    g4: LineSegment StartX=20 StartY=20 StartZ=0 EndX=1980 EndY=20 EndZ=0
    g5: LineSegment StartX=1980 StartY=20 StartZ=0 EndX=1980 EndY=2980 EndZ=0
    g6: LineSegment StartX=1980 StartY=2980 StartZ=0 EndX=20 EndY=2980 EndZ=0
    g7: LineSegment StartX=20 StartY=2980 StartZ=0 EndX=20 EndY=20 EndZ=0
  constraints (23):
    c: Coincident(g0,g1)
    c: Coincident(g1,g2)
    c: Coincident(g2,g3)
    c: Coincident(g3,g0)
    c: Horizontal(g0)
    c: Horizontal(g2)
    c: Vertical(g1)
    c: Vertical(g3)
    c: Coincident(g4,g5)
    c: Coincident(g5,g6)
    c: Coincident(g6,g7)
    c: Coincident(g7,g4)
    c: Horizontal(g4)
    c: Horizontal(g6)
    c: Vertical(g5)
    c: Vertical(g7)
    c: DistanceY(g1) = 3000  'Height'
    c: DistanceX(g0) = 2000  'Width'
    c: DistanceY(g6,g2) = 20  'Frame1'
    c: DistanceX(g2,g6) = 20  'Frame2'
    c: DistanceX(g4,g0) = 20  'Frame3'
    c: DistanceY(g0,g4) = 20  'Frame4'
    c: Coincident(g0,g-1)
FEATURE [Part::FeaturePython] Window007  label="Window 200x300"  # Arch/BIM 154 (typed FeaturePython)
  Area = 6000000
  Base = -> Sketch005
  Frame = 20
  Height = 3000
  HoleDepth = 0
  HoleWire = 0
  HorizontalArea = 0
  IfcData = IfcUID=0ObaA4RqaHwRzx093rt3ko,+1 more (map truncated)
  IfcType = 154
  LouvreSpacing = 0
  LouvreWidth = 0
  MoveBase = false
  MoveWithHost = true
  Normal = (-1,0,0)
  Opening = 0
  OverallHeight = 3000
  OverallWidth = 2000
  PartitioningType = 0
  PerimeterLength = 0
  Placement = pos=(-20200,-19425.3,0) rot=(0,0,-1;1.5708rad)
  PredefinedType = 0
  Preset = 1
  SymbolElevation = false
  SymbolPlan = false
  VerticalArea = 0
  Width = 2000
  WindowParts = OuterFrame | Frame | Wire0,Wire1 | 30.0+V | 0.0+V | Glass | Glass panel | Wire1 | 2.0 | 10.0+V
  expr: OverallWidth = Width.Value
  expr: OverallHeight = Height.Value
FEATURE [Sketcher::SketchObject] Sketch006
  Placement = pos=(-18700,-900,0) rot=(1,0,0;1.5708rad)
  sketch-geometry (8):
    g0: LineSegment StartX=0 StartY=0 StartZ=0 EndX=1950 EndY=0 EndZ=0
    g1: LineSegment StartX=1950 StartY=0 StartZ=0 EndX=1950 EndY=3000 EndZ=0
    g2: LineSegment StartX=1950 StartY=3000 StartZ=0 EndX=0 EndY=3000 EndZ=0
    g3: LineSegment StartX=0 StartY=3000 StartZ=0 EndX=0 EndY=0 EndZ=0
    g4: LineSegment StartX=20 StartY=20 StartZ=0 EndX=1930 EndY=20 EndZ=0
    g5: LineSegment StartX=1930 StartY=20 StartZ=0 EndX=1930 EndY=2980 EndZ=0
    g6: LineSegment StartX=1930 StartY=2980 StartZ=0 EndX=20 EndY=2980 EndZ=0
    g7: LineSegment StartX=20 StartY=2980 StartZ=0 EndX=20 EndY=20 EndZ=0
  constraints (23):
    c: Coincident(g0,g1)
    c: Coincident(g1,g2)
    c: Coincident(g2,g3)
    c: Coincident(g3,g0)
    c: Horizontal(g0)
    c: Horizontal(g2)
    c: Vertical(g1)
    c: Vertical(g3)
    c: Coincident(g4,g5)
    c: Coincident(g5,g6)
    c: Coincident(g6,g7)
    c: Coincident(g7,g4)
    c: Horizontal(g4)
    c: Horizontal(g6)
    c: Vertical(g5)
    c: Vertical(g7)
    c: DistanceY(g1) = 3000  'Height'
    c: DistanceX(g0) = 1950  'Width'
    c: DistanceY(g6,g2) = 20  'Frame1'
    c: DistanceX(g2,g6) = 20  'Frame2'
    c: DistanceX(g4,g0) = 20  'Frame3'
    c: DistanceY(g0,g4) = 20  'Frame4'
    c: Coincident(g0,g-1)
FEATURE [Part::FeaturePython] Window008  label="Window 195x300"  # Arch/BIM 154 (typed FeaturePython)
  Area = 5850000
  Base = -> Sketch006
  Frame = 20
  Height = 3000
  HoleDepth = 0
  HoleWire = 0
  HorizontalArea = 0
  IfcData = IfcUID=0OcJHERqaHwRzx093rt3ko,+1 more (map truncated)
  IfcType = 154
  LouvreSpacing = 0
  LouvreWidth = 0
  MoveBase = false
  MoveWithHost = true
  Normal = (0,1,-2e-16)
  Opening = 0
  OverallHeight = 3000
  OverallWidth = 1950
  PartitioningType = 0
  PerimeterLength = 0
  Placement = pos=(-1300,1874.66,0) rot=(0,0,1;0rad)
  PredefinedType = 0
  Preset = 1
  SymbolElevation = false
  SymbolPlan = false
  VerticalArea = 0
  Width = 1950
  WindowParts = OuterFrame | Frame | Wire0,Wire1 | 30.0+V | 0.00+V | Glass | Glass panel | Wire1 | 6.0 | 30.0+V
  expr: OverallWidth = Width.Value
  expr: OverallHeight = Height.Value
FEATURE [Sketcher::SketchObject] Sketch008
  Placement = pos=(-17950,974.662,0) rot=(1,0,0;1.5708rad)
  sketch-geometry (8):
    g0: LineSegment StartX=0 StartY=0 StartZ=0 EndX=1975 EndY=0 EndZ=0
    g1: LineSegment StartX=1975 StartY=0 StartZ=0 EndX=1975 EndY=3000 EndZ=0
    g2: LineSegment StartX=1975 StartY=3000 StartZ=0 EndX=0 EndY=3000 EndZ=0
    g3: LineSegment StartX=0 StartY=3000 StartZ=0 EndX=0 EndY=0 EndZ=0
    g4: LineSegment StartX=30 StartY=30 StartZ=0 EndX=1945 EndY=30 EndZ=0
    g5: LineSegment StartX=1945 StartY=30 StartZ=0 EndX=1945 EndY=2970 EndZ=0
    g6: LineSegment StartX=1945 StartY=2970 StartZ=0 EndX=30 EndY=2970 EndZ=0
    g7: LineSegment StartX=30 StartY=2970 StartZ=0 EndX=30 EndY=30 EndZ=0
  constraints (23):
    c: Coincident(g0,g1)
    c: Coincident(g1,g2)
    c: Coincident(g2,g3)
    c: Coincident(g3,g0)
    c: Horizontal(g0)
    c: Horizontal(g2)
    c: Vertical(g1)
    c: Vertical(g3)
    c: Coincident(g4,g5)
    c: Coincident(g5,g6)
    c: Coincident(g6,g7)
    c: Coincident(g7,g4)
    c: Horizontal(g4)
    c: Horizontal(g6)
    c: Vertical(g5)
    c: Vertical(g7)
    c: DistanceY(g1) = 3000  'Height'
    c: DistanceX(g0) = 1975  'Width'
    c: DistanceY(g6,g2) = 30  'Frame1'
    c: DistanceX(g2,g6) = 30  'Frame2'
    c: DistanceX(g4,g0) = 30  'Frame3'
    c: DistanceY(g0,g4) = 30  'Frame4'
    c: Coincident(g0,g-1)
FEATURE [Part::FeaturePython] Window009  label="Window 197x300"  # Arch/BIM 154 (typed FeaturePython)
  Area = 5925000
  Base = -> Sketch008
  Frame = 30
  Height = 3000
  HoleDepth = 0
  HoleWire = 0
  HorizontalArea = 0
  IfcData = IfcUID=0Od7rwRqaHwRzx093rt3ko,+1 more (map truncated)
  IfcType = 154
  LouvreSpacing = 0
  LouvreWidth = 0
  MoveBase = false
  MoveWithHost = true
  Normal = (0,1,-2e-16)
  Opening = 0
  OverallHeight = 3000
  OverallWidth = 1975
  PartitioningType = 0
  PerimeterLength = 0
  PredefinedType = 0
  Preset = 1
  SymbolElevation = false
  SymbolPlan = false
  VerticalArea = 0
  Width = 1975
  WindowParts = OuterFrame | Frame | Wire0,Wire1 | 30.0+V | 0.00+V | Glass | Glass panel | Wire1 | 6.0 | 30.0+V
  expr: OverallWidth = Width.Value
  expr: OverallHeight = Height.Value
FEATURE [Sketcher::SketchObject] Sketch009
  Placement = pos=(-15025,974.662,0) rot=(1,0,0;1.5708rad)
  sketch-geometry (8):
    g0: LineSegment StartX=0 StartY=0 StartZ=0 EndX=1025 EndY=0 EndZ=0
    g1: LineSegment StartX=1025 StartY=0 StartZ=0 EndX=1025 EndY=3000 EndZ=0
    g2: LineSegment StartX=1025 StartY=3000 StartZ=0 EndX=0 EndY=3000 EndZ=0
    g3: LineSegment StartX=0 StartY=3000 StartZ=0 EndX=0 EndY=0 EndZ=0
    g4: LineSegment StartX=30 StartY=30 StartZ=0 EndX=995 EndY=30 EndZ=0
    g5: LineSegment StartX=995 StartY=30 StartZ=0 EndX=995 EndY=2970 EndZ=0
    g6: LineSegment StartX=995 StartY=2970 StartZ=0 EndX=30 EndY=2970 EndZ=0
    g7: LineSegment StartX=30 StartY=2970 StartZ=0 EndX=30 EndY=30 EndZ=0
  constraints (23):
    c: Coincident(g0,g1)
    c: Coincident(g1,g2)
    c: Coincident(g2,g3)
    c: Coincident(g3,g0)
    c: Horizontal(g0)
    c: Horizontal(g2)
    c: Vertical(g1)
    c: Vertical(g3)
    c: Coincident(g4,g5)
    c: Coincident(g5,g6)
    c: Coincident(g6,g7)
    c: Coincident(g7,g4)
    c: Horizontal(g4)
    c: Horizontal(g6)
    c: Vertical(g5)
    c: Vertical(g7)
    c: DistanceY(g1) = 3000  'Height'
    c: DistanceX(g0) = 1025  'Width'
    c: DistanceY(g6,g2) = 30  'Frame1'
    c: DistanceX(g2,g6) = 30  'Frame2'
    c: DistanceX(g4,g0) = 30  'Frame3'
    c: DistanceY(g0,g4) = 30  'Frame4'
    c: Coincident(g0,g-1)
FEATURE [Part::FeaturePython] Window010  label="Window 102x300"  # Arch/BIM 154 (typed FeaturePython)
  Area = 3075000
  Base = -> Sketch009
  Frame = 30
  Height = 3000
  HoleDepth = 0
  HoleWire = 0
  HorizontalArea = 0
  IfcData = IfcUID=0OdvKARqaHwRzx093rt3ko,+1 more (map truncated)
  IfcType = 154
  LouvreSpacing = 0
  LouvreWidth = 0
  MoveBase = false
  MoveWithHost = true
  Normal = (0,1,-2e-16)
  Opening = 0
  OverallHeight = 3000
  OverallWidth = 1025
  PartitioningType = 0
  PerimeterLength = 0
  PredefinedType = 0
  Preset = 1
  SymbolElevation = false
  SymbolPlan = false
  VerticalArea = 0
  Width = 1025
  WindowParts = OuterFrame | Frame | Wire0,Wire1 | 30.0+V | 0.00+V | Glass | Glass panel | Wire1 | 6.0 | 30.0+V
  expr: OverallWidth = Width.Value
  expr: OverallHeight = Height.Value
FEATURE [Sketcher::SketchObject] Sketch010
  Placement = pos=(-15975,974.662,2100) rot=(1,0,0;1.5708rad)
  sketch-geometry (8):
    g0: LineSegment StartX=0 StartY=0 StartZ=0 EndX=950 EndY=0 EndZ=0
    g1: LineSegment StartX=950 StartY=0 StartZ=0 EndX=950 EndY=900 EndZ=0
    g2: LineSegment StartX=950 StartY=900 StartZ=0 EndX=0 EndY=900 EndZ=0
    g3: LineSegment StartX=0 StartY=900 StartZ=0 EndX=0 EndY=0 EndZ=0
    g4: LineSegment StartX=30 StartY=30 StartZ=0 EndX=920 EndY=30 EndZ=0
    g5: LineSegment StartX=920 StartY=30 StartZ=0 EndX=920 EndY=870 EndZ=0
    g6: LineSegment StartX=920 StartY=870 StartZ=0 EndX=30 EndY=870 EndZ=0
    g7: LineSegment StartX=30 StartY=870 StartZ=0 EndX=30 EndY=30 EndZ=0
  constraints (23):
    c: Coincident(g0,g1)
    c: Coincident(g1,g2)
    c: Coincident(g2,g3)
    c: Coincident(g3,g0)
    c: Horizontal(g0)
    c: Horizontal(g2)
    c: Vertical(g1)
    c: Vertical(g3)
    c: Coincident(g4,g5)
    c: Coincident(g5,g6)
    c: Coincident(g6,g7)
    c: Coincident(g7,g4)
    c: Horizontal(g4)
    c: Horizontal(g6)
    c: Vertical(g5)
    c: Vertical(g7)
    c: DistanceY(g1) = 900  'Height'
    c: DistanceX(g0) = 950  'Width'
    c: DistanceY(g6,g2) = 30  'Frame1'
    c: DistanceX(g2,g6) = 30  'Frame2'
    c: DistanceX(g4,g0) = 30  'Frame3'
    c: DistanceY(g0,g4) = 30  'Frame4'
    c: Coincident(g0,g-1)
FEATURE [Part::FeaturePython] Window011  label="Window top 95x90"  # Arch/BIM 154 (typed FeaturePython)
  Area = 855000
  Base = -> Sketch010
  Frame = 30
  Height = 900
  HoleDepth = 0
  HoleWire = 0
  HorizontalArea = 0
  IfcData = IfcUID=0OfZrgRqaHwRzx093rt3ko,+1 more (map truncated)
  IfcType = 154
  LouvreSpacing = 0
  LouvreWidth = 0
  MoveBase = false
  MoveWithHost = true
  Normal = (0,1,-2e-16)
  Opening = 0
  OverallHeight = 900
  OverallWidth = 950
  PartitioningType = 0
  PerimeterLength = 0
  PredefinedType = 0
  Preset = 1
  SymbolElevation = false
  SymbolPlan = false
  VerticalArea = 0
  Width = 950
  WindowParts = OuterFrame | Frame | Wire0,Wire1 | 30.0+V | 0.00+V | Glass | Glass panel | Wire1 | 6.0 | 30.0+V
  expr: OverallWidth = Width.Value
  expr: OverallHeight = Height.Value
FEATURE [Sketcher::SketchObject] Sketch011
  Placement = pos=(7000,-2380,0) rot=(1,0,0;1.5708rad)
  sketch-geometry (8):
    g0: LineSegment StartX=0 StartY=0 StartZ=0 EndX=1000 EndY=0 EndZ=0
    g1: LineSegment StartX=1000 StartY=0 StartZ=0 EndX=1000 EndY=3000 EndZ=0
    g2: LineSegment StartX=1000 StartY=3000 StartZ=0 EndX=0 EndY=3000 EndZ=0
    g3: LineSegment StartX=0 StartY=3000 StartZ=0 EndX=0 EndY=0 EndZ=0
    g4: LineSegment StartX=30 StartY=30 StartZ=0 EndX=970 EndY=30 EndZ=0
    g5: LineSegment StartX=970 StartY=30 StartZ=0 EndX=970 EndY=2970 EndZ=0
    g6: LineSegment StartX=970 StartY=2970 StartZ=0 EndX=30 EndY=2970 EndZ=0
    g7: LineSegment StartX=30 StartY=2970 StartZ=0 EndX=30 EndY=30 EndZ=0
  constraints (23):
    c: Coincident(g0,g1)
    c: Coincident(g1,g2)
    c: Coincident(g2,g3)
    c: Coincident(g3,g0)
    c: Horizontal(g0)
    c: Horizontal(g2)
    c: Vertical(g1)
    c: Vertical(g3)
    c: Coincident(g4,g5)
    c: Coincident(g5,g6)
    c: Coincident(g6,g7)
    c: Coincident(g7,g4)
    c: Horizontal(g4)
    c: Horizontal(g6)
    c: Vertical(g5)
    c: Vertical(g7)
    c: DistanceY(g1) = 3000  'Height'
    c: DistanceX(g0) = 1000  'Width'
    c: DistanceY(g6,g2) = 30  'Frame1'
    c: DistanceX(g2,g6) = 30  'Frame2'
    c: DistanceX(g4,g0) = 30  'Frame3'
    c: DistanceY(g0,g4) = 30  'Frame4'
    c: Coincident(g0,g-1)
FEATURE [Part::FeaturePython] Window012  label="Window 100x300 009"  # Arch/BIM 154 (typed FeaturePython)
  Area = 3000000
  Base = -> Sketch011
  Frame = 30
  Height = 3000
  HoleDepth = 0
  HoleWire = 0
  HorizontalArea = 0
  IfcData = IfcUID=0ObT1gRqaHwRzx093rt3ko,+1 more (map truncated)
  IfcType = 154
  LouvreSpacing = 0
  LouvreWidth = 0
  MoveBase = false
  MoveWithHost = true
  Normal = (0,1,-2e-16)
  Opening = 0
  OverallHeight = 3000
  OverallWidth = 1000
  PartitioningType = 0
  PerimeterLength = 0
  PredefinedType = 0
  Preset = 1
  SymbolElevation = false
  SymbolPlan = false
  VerticalArea = 0
  Width = 1000
  WindowParts = OuterFrame | Frame | Wire0,Wire1 | 20.0+V | 0.0+V | Glass | Glass panel | Wire1 | 6.0 | 30.0+V
  expr: OverallWidth = Width.Value
  expr: OverallHeight = Height.Value
FEATURE [Part::FeaturePython] Window013  label="Window 100x300 008"  # Arch/BIM 154 (typed FeaturePython)
  Area = 3000000
  CloneOf = -> Window012
  Frame = 0
  Height = 3000
  HoleDepth = 0
  HoleWire = 0
  HorizontalArea = 0
  IfcData = IfcUID=0ObM0IRqaHwRzx093rt3ko,+1 more (map truncated)
  IfcType = 154
  LouvreSpacing = 0
  LouvreWidth = 0
  MoveBase = false
  MoveWithHost = true
  Normal = (0,0,0)
  Opening = 0
  OverallHeight = 3000
  OverallWidth = 1000
  PartitioningType = 0
  PerimeterLength = 0
  Placement = pos=(1000,0,0) rot=(0,0,1;0rad)
  PredefinedType = 0
  Preset = 0
  SymbolElevation = false
  SymbolPlan = false
  VerticalArea = 0
  Width = 1000
  expr: OverallWidth = Width.Value
  expr: OverallHeight = Height.Value
FEATURE [Part::FeaturePython] Window014  label="Window 100x300 007"  # Arch/BIM 154 (typed FeaturePython)
  Area = 3000000
  CloneOf = -> Window012
  Frame = 0
  Height = 3000
  HoleDepth = 0
  HoleWire = 0
  HorizontalArea = 0
  IfcData = IfcUID=0ObF3SRqaHwRzx093rt3ko,+1 more (map truncated)
  IfcType = 154
  LouvreSpacing = 0
  LouvreWidth = 0
  MoveBase = false
  MoveWithHost = true
  Normal = (0,0,0)
  Opening = 0
  OverallHeight = 3000
  OverallWidth = 1000
  PartitioningType = 0
  PerimeterLength = 0
  Placement = pos=(2000,0,0) rot=(0,0,1;0rad)
  PredefinedType = 0
  Preset = 0
  SymbolElevation = false
  SymbolPlan = false
  VerticalArea = 0
  Width = 1000
  expr: OverallWidth = Width.Value
  expr: OverallHeight = Height.Value
FEATURE [Part::FeaturePython] Window015  label="Window 100x300 006"  # Arch/BIM 154 (typed FeaturePython)
  Area = 3000000
  CloneOf = -> Window012
  Frame = 0
  Height = 3000
  HoleDepth = 0
  HoleWire = 0
  HorizontalArea = 0
  IfcData = IfcUID=0Ob7y8RqaHwRzx093rt3ko,+1 more (map truncated)
  IfcType = 154
  LouvreSpacing = 0
  LouvreWidth = 0
  MoveBase = false
  MoveWithHost = true
  Normal = (0,0,0)
  Opening = 0
  OverallHeight = 3000
  OverallWidth = 1000
  PartitioningType = 0
  PerimeterLength = 0
  Placement = pos=(3000,4.55e-13,0) rot=(0,0,1;0rad)
  PredefinedType = 0
  Preset = 0
  SymbolElevation = false
  SymbolPlan = false
  VerticalArea = 0
  Width = 1000
  expr: OverallWidth = Width.Value
  expr: OverallHeight = Height.Value
FEATURE [Part::FeaturePython] Window016  label="Window 100x300 005"  # Arch/BIM 154 (typed FeaturePython)
  Area = 3000000
  CloneOf = -> Window012
  Frame = 0
  Height = 3000
  HoleDepth = 0
  HoleWire = 0
  HorizontalArea = 0
  IfcData = IfcUID=0Oa$tkRqaHwRzx093rt3ko,+1 more (map truncated)
  IfcType = 154
  LouvreSpacing = 0
  LouvreWidth = 0
  MoveBase = false
  MoveWithHost = true
  Normal = (0,0,0)
  Opening = 0
  OverallHeight = 3000
  OverallWidth = 1000
  PartitioningType = 0
  PerimeterLength = 0
  Placement = pos=(4000,9.09e-13,0) rot=(0,0,1;0rad)
  PredefinedType = 0
  Preset = 0
  SymbolElevation = false
  SymbolPlan = false
  VerticalArea = 0
  Width = 1000
  expr: OverallWidth = Width.Value
  expr: OverallHeight = Height.Value
FEATURE [Part::FeaturePython] Window017  label="Window 100x300 004"  # Arch/BIM 154 (typed FeaturePython)
  Area = 3000000
  CloneOf = -> Window012
  Frame = 0
  Height = 3000
  HoleDepth = 0
  HoleWire = 0
  HorizontalArea = 0
  IfcData = IfcUID=0OatFsRqaHwRzx093rt3ko,+1 more (map truncated)
  IfcType = 154
  LouvreSpacing = 0
  LouvreWidth = 0
  MoveBase = false
  MoveWithHost = true
  Normal = (0,0,0)
  Opening = 0
  OverallHeight = 3000
  OverallWidth = 1000
  PartitioningType = 0
  PerimeterLength = 0
  Placement = pos=(8000,1.819e-12,0) rot=(0,0,1;0rad)
  PredefinedType = 0
  Preset = 0
  SymbolElevation = false
  SymbolPlan = false
  VerticalArea = 0
  Width = 1000
  expr: OverallWidth = Width.Value
  expr: OverallHeight = Height.Value
FEATURE [Part::FeaturePython] Window018  label="Window 100x300 003"  # Arch/BIM 154 (typed FeaturePython)
  Area = 3000000
  CloneOf = -> Window012
  Frame = 0
  Height = 3000
  HoleDepth = 0
  HoleWire = 0
  HorizontalArea = 0
  IfcData = IfcUID=0OakeSRqaHwRzx093rt3ko,+1 more (map truncated)
  IfcType = 154
  LouvreSpacing = 0
  LouvreWidth = 0
  MoveBase = false
  MoveWithHost = true
  Normal = (0,0,0)
  Opening = 0
  OverallHeight = 3000
  OverallWidth = 1000
  PartitioningType = 0
  PerimeterLength = 0
  Placement = pos=(7000,1.3642e-12,0) rot=(0,0,1;0rad)
  PredefinedType = 0
  Preset = 0
  SymbolElevation = false
  SymbolPlan = false
  VerticalArea = 0
  Width = 1000
  expr: OverallWidth = Width.Value
  expr: OverallHeight = Height.Value
FEATURE [Part::FeaturePython] Window019  label="Window 100x300 002"  # Arch/BIM 154 (typed FeaturePython)
  Area = 3000000
  CloneOf = -> Window012
  Frame = 0
  Height = 3000
  HoleDepth = 0
  HoleWire = 0
  HorizontalArea = 0
  IfcData = IfcUID=0OabzIRqaHwRzx093rt3ko,+1 more (map truncated)
  IfcType = 154
  LouvreSpacing = 0
  LouvreWidth = 0
  MoveBase = false
  MoveWithHost = true
  Normal = (0,0,0)
  Opening = 0
  OverallHeight = 3000
  OverallWidth = 1000
  PartitioningType = 0
  PerimeterLength = 0
  Placement = pos=(9000,2.274e-12,0) rot=(0,0,1;0rad)
  PredefinedType = 0
  Preset = 0
  SymbolElevation = false
  SymbolPlan = false
  VerticalArea = 0
  Width = 1000
  expr: OverallWidth = Width.Value
  expr: OverallHeight = Height.Value
FEATURE [Part::FeaturePython] Window020  label="Window 100x300 001"  # Arch/BIM 154 (typed FeaturePython)
  Area = 3000000
  CloneOf = -> Window012
  Frame = 0
  Height = 3000
  HoleDepth = 0
  HoleWire = 0
  HorizontalArea = 0
  IfcData = IfcUID=0OaTL6RqaHwRzx093rt3ko,+1 more (map truncated)
  IfcType = 154
  LouvreSpacing = 0
  LouvreWidth = 0
  MoveBase = false
  MoveWithHost = true
  Normal = (0,0,0)
  Opening = 0
  OverallHeight = 3000
  OverallWidth = 1000
  PartitioningType = 0
  PerimeterLength = 0
  Placement = pos=(5000,1.3642e-12,0) rot=(0,0,1;0rad)
  PredefinedType = 0
  Preset = 0
  SymbolElevation = false
  SymbolPlan = false
  VerticalArea = 0
  Width = 1000
  expr: OverallWidth = Width.Value
  expr: OverallHeight = Height.Value
FEATURE [Part::FeaturePython] Window021  label="Window 100x300 "  # Arch/BIM 154 (typed FeaturePython)
  Area = 3000000
  CloneOf = -> Window012
  Frame = 0
  Height = 3000
  HoleDepth = 0
  HoleWire = 0
  HorizontalArea = 0
  IfcData = IfcUID=0OZfyWRqaHwRzx093rt3ko,+1 more (map truncated)
  IfcType = 154
  LouvreSpacing = 0
  LouvreWidth = 0
  MoveBase = false
  MoveWithHost = true
  Normal = (0,0,0)
  Opening = 0
  OverallHeight = 3000
  OverallWidth = 1000
  PartitioningType = 0
  PerimeterLength = 0
  Placement = pos=(6000,1.3642e-12,0) rot=(0,0,1;0rad)
  PredefinedType = 0
  Preset = 0
  SymbolElevation = false
  SymbolPlan = false
  VerticalArea = 0
  Width = 1000
  expr: OverallWidth = Width.Value
  expr: OverallHeight = Height.Value
FEATURE [Sketcher::SketchObject] Sketch012
  Placement = pos=(8400,-4500,0) rot=(1,0,0;1.5708rad)
  sketch-geometry (8):
    g0: LineSegment StartX=0 StartY=0 StartZ=0 EndX=3040 EndY=0 EndZ=0
    g1: LineSegment StartX=3040 StartY=0 StartZ=0 EndX=3040 EndY=3000 EndZ=0
    g2: LineSegment StartX=3040 StartY=3000 StartZ=0 EndX=0 EndY=3000 EndZ=0
    g3: LineSegment StartX=0 StartY=3000 StartZ=0 EndX=0 EndY=0 EndZ=0
    g4: LineSegment StartX=30 StartY=30 StartZ=0 EndX=3010 EndY=30 EndZ=0
    g5: LineSegment StartX=3010 StartY=30 StartZ=0 EndX=3010 EndY=2970 EndZ=0
    g6: LineSegment StartX=3010 StartY=2970 StartZ=0 EndX=30 EndY=2970 EndZ=0
    g7: LineSegment StartX=30 StartY=2970 StartZ=0 EndX=30 EndY=30 EndZ=0
  constraints (23):
    c: Coincident(g0,g1)
    c: Coincident(g1,g2)
    c: Coincident(g2,g3)
    c: Coincident(g3,g0)
    c: Horizontal(g0)
    c: Horizontal(g2)
    c: Vertical(g1)
    c: Vertical(g3)
    c: Coincident(g4,g5)
    c: Coincident(g5,g6)
    c: Coincident(g6,g7)
    c: Coincident(g7,g4)
    c: Horizontal(g4)
    c: Horizontal(g6)
    c: Vertical(g5)
    c: Vertical(g7)
    c: DistanceY(g1) = 3000  'Height'
    c: DistanceX(g0) = 3040  'Width'
    c: DistanceY(g6,g2) = 30  'Frame1'
    c: DistanceX(g2,g6) = 30  'Frame2'
    c: DistanceX(g4,g0) = 30  'Frame3'
    c: DistanceY(g0,g4) = 30  'Frame4'
    c: Coincident(g0,g-1)
FEATURE [Part::FeaturePython] Window022  label="Window 304x300 001"  # Arch/BIM 154 (typed FeaturePython)
  Area = 9120000
  Base = -> Sketch012
  Frame = 30
  Height = 3000
  HoleDepth = 0
  HoleWire = 0
  HorizontalArea = 0
  IfcData = IfcUID=0OYhIgRqaHwRzx093rt3ko,+1 more (map truncated)
  IfcType = 154
  LouvreSpacing = 0
  LouvreWidth = 0
  MoveBase = false
  MoveWithHost = true
  Normal = (0,1,-2e-16)
  Opening = 0
  OverallHeight = 3000
  OverallWidth = 3040
  PartitioningType = 0
  PerimeterLength = 0
  Placement = pos=(12470,6020,0) rot=(0,0,-1;1.5708rad)
  PredefinedType = 0
  Preset = 1
  SymbolElevation = false
  SymbolPlan = false
  VerticalArea = 0
  Width = 3040
  WindowParts = OuterFrame | Frame | Wire0,Wire1 | 30.0+V | 0.00+V | Glass | Glass panel | Wire1 | 6.0 | 30.0+V
  expr: OverallWidth = Width.Value
  expr: OverallHeight = Height.Value
FEATURE [Sketcher::SketchObject] Sketch013
  Placement = pos=(10400,-6400,0) rot=(1,0,0;1.5708rad)
  sketch-geometry (8):
    g0: LineSegment StartX=0 StartY=1.137e-13 StartZ=0 EndX=3090 EndY=1.137e-13 EndZ=0
    g1: LineSegment StartX=3090 StartY=1.137e-13 StartZ=0 EndX=3090 EndY=3000 EndZ=0
    g2: LineSegment StartX=3090 StartY=3000 StartZ=0 EndX=0 EndY=3000 EndZ=0
    g3: LineSegment StartX=0 StartY=3000 StartZ=0 EndX=0 EndY=0 EndZ=0
    g4: LineSegment StartX=30 StartY=30 StartZ=0 EndX=3060 EndY=30 EndZ=0
    g5: LineSegment StartX=3060 StartY=30 StartZ=0 EndX=3060 EndY=2970 EndZ=0
    g6: LineSegment StartX=3060 StartY=2970 StartZ=0 EndX=30 EndY=2970 EndZ=0
    g7: LineSegment StartX=30 StartY=2970 StartZ=0 EndX=30 EndY=30 EndZ=0
  constraints (23):
    c: Coincident(g0,g1)
    c: Coincident(g1,g2)
    c: Coincident(g2,g3)
    c: Coincident(g3,g0)
    c: Horizontal(g0)
    c: Horizontal(g2)
    c: Vertical(g1)
    c: Vertical(g3)
    c: Coincident(g4,g5)
    c: Coincident(g5,g6)
    c: Coincident(g6,g7)
    c: Coincident(g7,g4)
    c: Horizontal(g4)
    c: Horizontal(g6)
    c: Vertical(g5)
    c: Vertical(g7)
    c: DistanceY(g1) = 3000  'Height'
    c: DistanceX(g0) = 3090  'Width'
    c: DistanceY(g6,g2) = 30  'Frame1'
    c: DistanceX(g2,g6) = 30  'Frame2'
    c: DistanceX(g4,g0) = 30  'Frame3'
    c: DistanceY(g0,g4) = 30  'Frame4'
    c: Coincident(g0,g-1)
FEATURE [Part::FeaturePython] Window023  label="Window 309x300 001"  # Arch/BIM 154 (typed FeaturePython)
  Area = 9270000
  Base = -> Sketch013
  Frame = 30
  Height = 3000
  HoleDepth = 0
  HoleWire = 0
  HorizontalArea = 0
  IfcData = IfcUID=0OZYKERqaHwRzx093rt3ko,+1 more (map truncated)
  IfcType = 154
  LouvreSpacing = 0
  LouvreWidth = 0
  MoveBase = false
  MoveWithHost = true
  Normal = (0,1,-2e-16)
  Opening = 0
  OverallHeight = 3000
  OverallWidth = 3090
  PartitioningType = 0
  PerimeterLength = 0
  Placement = pos=(14370,4980,0) rot=(0,0,-1;1.5708rad)
  PredefinedType = 0
  Preset = 1
  SymbolElevation = false
  SymbolPlan = false
  VerticalArea = 0
  Width = 3090
  WindowParts = OuterFrame | Frame | Wire0,Wire1 | 30.0+V | 0.00+V | Glass | Glass panel | Wire1 | 6.0 | 30.0+V
  expr: OverallWidth = Width.Value
  expr: OverallHeight = Height.Value
FEATURE [Part::FeaturePython] Window024  label="Window 309x300 "  # Arch/BIM 154 (typed FeaturePython)
  Area = 9270000
  CloneOf = -> Window023
  Frame = 0
  Height = 3000
  HoleDepth = 0
  HoleWire = 0
  HorizontalArea = 0
  IfcData = IfcUID=0OYpekRqaHwRzx093rt3ko,+1 more (map truncated)
  IfcType = 154
  LouvreSpacing = 0
  LouvreWidth = 0
  MoveBase = false
  MoveWithHost = true
  Normal = (0,0,0)
  Opening = 0
  OverallHeight = 3000
  OverallWidth = 3090
  PartitioningType = 0
  PerimeterLength = 0
  Placement = pos=(15370,4980,0) rot=(0,0,-1;1.5708rad)
  PredefinedType = 0
  Preset = 0
  SymbolElevation = false
  SymbolPlan = false
  VerticalArea = 0
  Width = 3090
  expr: OverallWidth = Width.Value
  expr: OverallHeight = Height.Value
FEATURE [Part::FeaturePython] Window025  label="Window 304x300 "  # Arch/BIM 154 (typed FeaturePython)
  Area = 9120000
  CloneOf = -> Window022
  Frame = 0
  Height = 3000
  HoleDepth = 0
  HoleWire = 0
  HorizontalArea = 0
  IfcData = IfcUID=0OWYWSRqaHwRzx093rt3ko,+1 more (map truncated)
  IfcType = 154
  LouvreSpacing = 0
  LouvreWidth = 0
  MoveBase = false
  MoveWithHost = true
  Normal = (0,0,0)
  Opening = 0
  OverallHeight = 3000
  OverallWidth = 3040
  PartitioningType = 0
  PerimeterLength = 0
  Placement = pos=(13470,6020,0) rot=(0,0,-1;1.5708rad)
  PredefinedType = 0
  Preset = 0
  SymbolElevation = false
  SymbolPlan = false
  VerticalArea = 0
  Width = 3040
  expr: OverallWidth = Width.Value
  expr: OverallHeight = Height.Value
FEATURE [Sketcher::SketchObject] Sketch014
  Placement = pos=(10700,-10300,0) rot=(1,0,0;1.5708rad)
  sketch-geometry (8):
    g0: LineSegment StartX=0 StartY=0 StartZ=0 EndX=3777.77 EndY=0 EndZ=0
    g1: LineSegment StartX=3777.77 StartY=0 StartZ=0 EndX=3777.77 EndY=3000 EndZ=0
    g2: LineSegment StartX=3777.77 StartY=3000 StartZ=0 EndX=0 EndY=3000 EndZ=0
    g3: LineSegment StartX=0 StartY=3000 StartZ=0 EndX=0 EndY=0 EndZ=0
    g4: LineSegment StartX=30 StartY=30 StartZ=0 EndX=3747.77 EndY=30 EndZ=0
    g5: LineSegment StartX=3747.77 StartY=30 StartZ=0 EndX=3747.77 EndY=2970 EndZ=0
    g6: LineSegment StartX=3747.77 StartY=2970 StartZ=0 EndX=30 EndY=2970 EndZ=0
    g7: LineSegment StartX=30 StartY=2970 StartZ=0 EndX=30 EndY=30 EndZ=0
  constraints (23):
    c: Coincident(g0,g1)
    c: Coincident(g1,g2)
    c: Coincident(g2,g3)
    c: Coincident(g3,g0)
    c: Horizontal(g0)
    c: Horizontal(g2)
    c: Vertical(g1)
    c: Vertical(g3)
    c: Coincident(g4,g5)
    c: Coincident(g5,g6)
    c: Coincident(g6,g7)
    c: Coincident(g7,g4)
    c: Horizontal(g4)
    c: Horizontal(g6)
    c: Vertical(g5)
    c: Vertical(g7)
    c: DistanceY(g1) = 3000  'Height'
    c: DistanceX(g0) = 3777.77  'Width'
    c: DistanceY(g6,g2) = 30  'Frame1'
    c: DistanceX(g2,g6) = 30  'Frame2'
    c: DistanceX(g4,g0) = 30  'Frame3'
    c: DistanceY(g0,g4) = 30  'Frame4'
    c: Coincident(g0,g-1)
FEATURE [Part::FeaturePython] Window026  label="Window 338x300 002"  # Arch/BIM 154 (typed FeaturePython)
  Area = 11333310
  Base = -> Sketch014
  Frame = 30
  Height = 3000
  HoleDepth = 0
  HoleWire = 0
  HorizontalArea = 0
  IfcData = IfcUID=0OWRCoRqaHwRzx093rt3ko,+1 more (map truncated)
  IfcType = 154
  LouvreSpacing = 0
  LouvreWidth = 0
  MoveBase = false
  MoveWithHost = true
  Normal = (0,1,-2e-16)
  Opening = 0
  OverallHeight = 3000
  OverallWidth = 3777.77
  PartitioningType = 0
  PerimeterLength = 0
  Placement = pos=(-3699.98,-760,0) rot=(0,0,1;0rad)
  PredefinedType = 0
  Preset = 1
  SymbolElevation = false
  SymbolPlan = false
  VerticalArea = 0
  Width = 3777.77
  WindowParts = OuterFrame | Frame | Wire0,Wire1 | 30.0+V | 0.00+V | Glass | Glass panel | Wire1 | 6.0 | 30.0+V
  expr: OverallWidth = Width.Value
  expr: OverallHeight = Height.Value
FEATURE [Part::FeaturePython] Window027  label="Window 338x300 001"  # Arch/BIM 154 (typed FeaturePython)
  Area = 11333310
  CloneOf = -> Window026
  Frame = 0
  Height = 3000
  HoleDepth = 0
  HoleWire = 0
  HorizontalArea = 0
  IfcData = IfcUID=0OWJKkRqaHwRzx093rt3ko,+1 more (map truncated)
  IfcType = 154
  LouvreSpacing = 0
  LouvreWidth = 0
  MoveBase = false
  MoveWithHost = true
  Normal = (0,0,0)
  Opening = 0
  OverallHeight = 3000
  OverallWidth = 3777.77
  PartitioningType = 0
  PerimeterLength = 0
  Placement = pos=(77.7934,-760,0) rot=(0,0,1;0rad)
  PredefinedType = 0
  Preset = 0
  SymbolElevation = false
  SymbolPlan = false
  VerticalArea = 0
  Width = 3777.77
  expr: OverallWidth = Width.Value
  expr: OverallHeight = Height.Value
FEATURE [Part::FeaturePython] Window028  label="Window 338x300 "  # Arch/BIM 154 (typed FeaturePython)
  Area = 11333310
  CloneOf = -> Window026
  Frame = 0
  Height = 3000
  HoleDepth = 0
  HoleWire = 0
  HorizontalArea = 0
  IfcData = IfcUID=0OVYDmRqaHwRzx093rt3ko,+1 more (map truncated)
  IfcType = 154
  LouvreSpacing = 0
  LouvreWidth = 0
  MoveBase = false
  MoveWithHost = true
  Normal = (0,0,0)
  Opening = 0
  OverallHeight = 3000
  OverallWidth = 3777.77
  PartitioningType = 0
  PerimeterLength = 0
  Placement = pos=(3855.56,-760,0) rot=(0,0,1;0rad)
  PredefinedType = 0
  Preset = 0
  SymbolElevation = false
  SymbolPlan = false
  VerticalArea = 0
  Width = 3777.77
  expr: OverallWidth = Width.Value
  expr: OverallHeight = Height.Value
FEATURE [Sketcher::SketchObject] Sketch015
  Placement = pos=(9100,-9500,0) rot=(1,0,0;1.5708rad)
  sketch-geometry (8):
    g0: LineSegment StartX=0 StartY=-1.137e-13 StartZ=0 EndX=330 EndY=-1.137e-13 EndZ=0
    g1: LineSegment StartX=330 StartY=-1.137e-13 StartZ=0 EndX=330 EndY=3000 EndZ=0
    g2: LineSegment StartX=330 StartY=3000 StartZ=0 EndX=0 EndY=3000 EndZ=0
    g3: LineSegment StartX=0 StartY=3000 StartZ=0 EndX=0 EndY=0 EndZ=0
    g4: LineSegment StartX=30 StartY=30 StartZ=0 EndX=300 EndY=30 EndZ=0
    g5: LineSegment StartX=300 StartY=30 StartZ=0 EndX=300 EndY=2970 EndZ=0
    g6: LineSegment StartX=300 StartY=2970 StartZ=0 EndX=30 EndY=2970 EndZ=0
    g7: LineSegment StartX=30 StartY=2970 StartZ=0 EndX=30 EndY=30 EndZ=0
  constraints (23):
    c: Coincident(g0,g1)
    c: Coincident(g1,g2)
    c: Coincident(g2,g3)
    c: Coincident(g3,g0)
    c: Horizontal(g0)
    c: Horizontal(g2)
    c: Vertical(g1)
    c: Vertical(g3)
    c: Coincident(g4,g5)
    c: Coincident(g5,g6)
    c: Coincident(g6,g7)
    c: Coincident(g7,g4)
    c: Horizontal(g4)
    c: Horizontal(g6)
    c: Vertical(g5)
    c: Vertical(g7)
    c: DistanceY(g1) = 3000  'Height'
    c: DistanceX(g0) = 330  'Width'
    c: DistanceY(g6,g2) = 30  'Frame1'
    c: DistanceX(g2,g6) = 30  'Frame2'
    c: DistanceX(g4,g0) = 30  'Frame3'
    c: DistanceY(g0,g4) = 30  'Frame4'
    c: Coincident(g0,g-1)
FEATURE [Part::FeaturePython] Window029  label="Window 33x300 001"  # Arch/BIM 154 (typed FeaturePython)
  Area = 990000
  Base = -> Sketch015
  Frame = 30
  Height = 3000
  HoleDepth = 0
  HoleWire = 0
  HorizontalArea = 0
  IfcData = IfcUID=0OVPMkRqaHwRzx093rt3ko,+1 more (map truncated)
  IfcType = 154
  LouvreSpacing = 0
  LouvreWidth = 0
  MoveBase = false
  MoveWithHost = true
  Normal = (0,1,-2e-16)
  Opening = 0
  OverallHeight = 3000
  OverallWidth = 330
  PartitioningType = 0
  PerimeterLength = 0
  Placement = pos=(16500,430,0) rot=(0,0,-1;1.5708rad)
  PredefinedType = 0
  Preset = 1
  SymbolElevation = false
  SymbolPlan = false
  VerticalArea = 0
  Width = 330
  WindowParts = OuterFrame | Frame | Wire0,Wire1 | 30.0+V | 0.00+V | Glass | Glass panel | Wire1 | 6.0 | 30.0+V
  expr: OverallWidth = Width.Value
  expr: OverallHeight = Height.Value
FEATURE [Sketcher::SketchObject] Sketch016
  Placement = pos=(7000,-9000,2100) rot=(0.57735,-0.57735,-0.57735;2.0944rad)
  sketch-geometry (8):
    g0: LineSegment StartX=0 StartY=0 StartZ=0 EndX=2000 EndY=0 EndZ=0
    g1: LineSegment StartX=2000 StartY=0 StartZ=0 EndX=2000 EndY=900 EndZ=0
    g2: LineSegment StartX=2000 StartY=900 StartZ=0 EndX=0 EndY=900 EndZ=0
    g3: LineSegment StartX=0 StartY=900 StartZ=0 EndX=0 EndY=0 EndZ=0
    g4: LineSegment StartX=30 StartY=30 StartZ=0 EndX=1970 EndY=30 EndZ=0
    g5: LineSegment StartX=1970 StartY=30 StartZ=0 EndX=1970 EndY=870 EndZ=0
    g6: LineSegment StartX=1970 StartY=870 StartZ=0 EndX=30 EndY=870 EndZ=0
    g7: LineSegment StartX=30 StartY=870 StartZ=0 EndX=30 EndY=30 EndZ=0
  constraints (23):
    c: Coincident(g0,g1)
    c: Coincident(g1,g2)
    c: Coincident(g2,g3)
    c: Coincident(g3,g0)
    c: Horizontal(g0)
    c: Horizontal(g2)
    c: Vertical(g1)
    c: Vertical(g3)
    c: Coincident(g4,g5)
    c: Coincident(g5,g6)
    c: Coincident(g6,g7)
    c: Coincident(g7,g4)
    c: Horizontal(g4)
    c: Horizontal(g6)
    c: Vertical(g5)
    c: Vertical(g7)
    c: DistanceY(g1) = 900  'Height'
    c: DistanceX(g0) = 2000  'Width'
    c: DistanceY(g6,g2) = 30  'Frame1'
    c: DistanceX(g2,g6) = 30  'Frame2'
    c: DistanceX(g4,g0) = 30  'Frame3'
    c: DistanceY(g0,g4) = 30  'Frame4'
    c: Coincident(g0,g-1)
FEATURE [Part::FeaturePython] Window030  label="Window top 200x90 "  # Arch/BIM 154 (typed FeaturePython)
  Area = 1800000
  Base = -> Sketch016
  Frame = 30
  Height = 900
  HoleDepth = 0
  HoleWire = 0
  HorizontalArea = 0
  IfcData = IfcUID=0OfRHERqaHwRzx093rt3ko,+1 more (map truncated)
  IfcType = 154
  LouvreSpacing = 0
  LouvreWidth = 0
  MoveBase = false
  MoveWithHost = true
  Normal = (1,0,0)
  Opening = 0
  OverallHeight = 900
  OverallWidth = 2000
  PartitioningType = 0
  PerimeterLength = 0
  PredefinedType = 0
  Preset = 1
  SymbolElevation = false
  SymbolPlan = false
  VerticalArea = 0
  Width = 2000
  WindowParts = OuterFrame | Frame | Wire0,Wire1 | 30.0+V | 0.00+V | Glass | Glass panel | Wire1 | 6.0 | 30.0+V
  expr: OverallWidth = Width.Value
  expr: OverallHeight = Height.Value
FEATURE [Part::FeaturePython] Window031  label="Window top 200x90 001"  # Arch/BIM 154 (typed FeaturePython)
  Area = 1800000
  CloneOf = -> Window030
  Frame = 0
  Height = 900
  HoleDepth = 0
  HoleWire = 0
  HorizontalArea = 0
  IfcData = IfcUID=0OeeCURqaHwRzx093rt3ko,+1 more (map truncated)
  IfcType = 154
  LouvreSpacing = 0
  LouvreWidth = 0
  MoveBase = false
  MoveWithHost = true
  Normal = (0,0,0)
  Opening = 0
  OverallHeight = 900
  OverallWidth = 2000
  PartitioningType = 0
  PerimeterLength = 0
  Placement = pos=(8970,9000,0) rot=(0,0,1;0rad)
  PredefinedType = 0
  Preset = 0
  SymbolElevation = false
  SymbolPlan = false
  VerticalArea = 0
  Width = 2000
  expr: OverallWidth = Width.Value
  expr: OverallHeight = Height.Value
FEATURE [Part::FeaturePython] Window032  label="Window 33x300 "  # Arch/BIM 154 (typed FeaturePython)
  Area = 990000
  CloneOf = -> Window029
  Frame = 0
  Height = 3000
  HoleDepth = 0
  HoleWire = 0
  HorizontalArea = 0
  IfcData = IfcUID=0OUalsRqaHwRzx093rt3ko,+1 more (map truncated)
  IfcType = 154
  LouvreSpacing = 0
  LouvreWidth = 0
  MoveBase = false
  MoveWithHost = true
  Normal = (0,0,0)
  Opening = 0
  OverallHeight = 3000
  OverallWidth = 330
  PartitioningType = 0
  PerimeterLength = 0
  Placement = pos=(25470,7100,0) rot=(0,0,-1;1.5708rad)
  PredefinedType = 0
  Preset = 0
  SymbolElevation = false
  SymbolPlan = false
  VerticalArea = 0
  Width = 330
  expr: OverallWidth = Width.Value
  expr: OverallHeight = Height.Value
FEATURE [Sketcher::SketchObject] Sketch017
  Placement = pos=(22400,-2500,0) rot=(1,0,0;1.5708rad)
  sketch-geometry (8):
    g0: LineSegment StartX=0 StartY=0 StartZ=0 EndX=895 EndY=0 EndZ=0
    g1: LineSegment StartX=895 StartY=0 StartZ=0 EndX=895 EndY=3000 EndZ=0
    g2: LineSegment StartX=895 StartY=3000 StartZ=0 EndX=0 EndY=3000 EndZ=0
    g3: LineSegment StartX=0 StartY=3000 StartZ=0 EndX=0 EndY=0 EndZ=0
    g4: LineSegment StartX=30 StartY=30 StartZ=0 EndX=865 EndY=30 EndZ=0
    g5: LineSegment StartX=865 StartY=30 StartZ=0 EndX=865 EndY=2970 EndZ=0
    g6: LineSegment StartX=865 StartY=2970 StartZ=0 EndX=30 EndY=2970 EndZ=0
    g7: LineSegment StartX=30 StartY=2970 StartZ=0 EndX=30 EndY=30 EndZ=0
  constraints (23):
    c: Coincident(g0,g1)
    c: Coincident(g1,g2)
    c: Coincident(g2,g3)
    c: Coincident(g3,g0)
    c: Horizontal(g0)
    c: Horizontal(g2)
    c: Vertical(g1)
    c: Vertical(g3)
    c: Coincident(g4,g5)
    c: Coincident(g5,g6)
    c: Coincident(g6,g7)
    c: Coincident(g7,g4)
    c: Horizontal(g4)
    c: Horizontal(g6)
    c: Vertical(g5)
    c: Vertical(g7)
    c: DistanceY(g1) = 3000  'Height'
    c: DistanceX(g0) = 895  'Width'
    c: DistanceY(g6,g2) = 30  'Frame1'
    c: DistanceX(g2,g6) = 30  'Frame2'
    c: DistanceX(g4,g0) = 30  'Frame3'
    c: DistanceY(g0,g4) = 30  'Frame4'
    c: Coincident(g0,g-1)
FEATURE [Part::FeaturePython] Window033  label="Window 89x300 007"  # Arch/BIM 154 (typed FeaturePython)
  Area = 2685000
  Base = -> Sketch017
  Frame = 30
  Height = 3000
  HoleDepth = 0
  HoleWire = 0
  HorizontalArea = 0
  IfcData = IfcUID=0OT1VWRqaHwRzx093rt3ko,+1 more (map truncated)
  IfcType = 154
  LouvreSpacing = 0
  LouvreWidth = 0
  MoveBase = false
  MoveWithHost = true
  Normal = (0,1,-2e-16)
  Opening = 0
  OverallHeight = 3000
  OverallWidth = 895
  PartitioningType = 0
  PerimeterLength = 0
  Placement = pos=(24250,20480,0) rot=(0,0,-1;1.5708rad)
  PredefinedType = 0
  Preset = 1
  SymbolElevation = false
  SymbolPlan = false
  VerticalArea = 0
  Width = 895
  WindowParts = OuterFrame | Frame | Wire0,Wire1 | 30.0+V | 0.00+V | Glass | Glass panel | Wire1 | 6.0 | 30.0+V
  expr: OverallWidth = Width.Value
  expr: OverallHeight = Height.Value
FEATURE [Part::FeaturePython] Window034  label="Window 89x300 006"  # Arch/BIM 154 (typed FeaturePython)
  Area = 2685000
  CloneOf = -> Window033
  Frame = 0
  Height = 3000
  HoleDepth = 0
  HoleWire = 0
  HorizontalArea = 0
  IfcData = IfcUID=0OTopmRqaHwRzx093rt3ko,+1 more (map truncated)
  IfcType = 154
  LouvreSpacing = 0
  LouvreWidth = 0
  MoveBase = false
  MoveWithHost = true
  Normal = (0,0,0)
  Opening = 0
  OverallHeight = 3000
  OverallWidth = 895
  PartitioningType = 0
  PerimeterLength = 0
  Placement = pos=(24250,19585,0) rot=(0,0,-1;1.5708rad)
  PredefinedType = 0
  Preset = 0
  SymbolElevation = false
  SymbolPlan = false
  VerticalArea = 0
  Width = 895
  expr: OverallWidth = Width.Value
  expr: OverallHeight = Height.Value
FEATURE [Part::FeaturePython] Window035  label="Window 89x300 005"  # Arch/BIM 154 (typed FeaturePython)
  Area = 2685000
  CloneOf = -> Window033
  Frame = 0
  Height = 3000
  HoleDepth = 0
  HoleWire = 0
  HorizontalArea = 0
  IfcData = IfcUID=0OTwdIRqaHwRzx093rt3ko,+1 more (map truncated)
  IfcType = 154
  LouvreSpacing = 0
  LouvreWidth = 0
  MoveBase = false
  MoveWithHost = true
  Normal = (0,0,0)
  Opening = 0
  OverallHeight = 3000
  OverallWidth = 895
  PartitioningType = 0
  PerimeterLength = 0
  Placement = pos=(24250,18690,0) rot=(0,0,-1;1.5708rad)
  PredefinedType = 0
  Preset = 0
  SymbolElevation = false
  SymbolPlan = false
  VerticalArea = 0
  Width = 895
  expr: OverallWidth = Width.Value
  expr: OverallHeight = Height.Value
FEATURE [Part::FeaturePython] Window036  label="Window 89x300 004"  # Arch/BIM 154 (typed FeaturePython)
  Area = 2685000
  CloneOf = -> Window033
  Frame = 0
  Height = 3000
  HoleDepth = 0
  HoleWire = 0
  HorizontalArea = 0
  IfcData = IfcUID=0OU1eCRqaHwRzx093rt3ko,+1 more (map truncated)
  IfcType = 154
  LouvreSpacing = 0
  LouvreWidth = 0
  MoveBase = false
  MoveWithHost = true
  Normal = (0,0,0)
  Opening = 0
  OverallHeight = 3000
  OverallWidth = 895
  PartitioningType = 0
  PerimeterLength = 0
  Placement = pos=(24250,17795,0) rot=(0,0,-1;1.5708rad)
  PredefinedType = 0
  Preset = 0
  SymbolElevation = false
  SymbolPlan = false
  VerticalArea = 0
  Width = 895
  expr: OverallWidth = Width.Value
  expr: OverallHeight = Height.Value
FEATURE [Part::FeaturePython] Window037  label="Window 89x300 003"  # Arch/BIM 154 (typed FeaturePython)
  Area = 2685000
  CloneOf = -> Window033
  Frame = 0
  Height = 3000
  HoleDepth = 0
  HoleWire = 0
  HorizontalArea = 0
  IfcData = IfcUID=0OU8ccRqaHwRzx093rt3ko,+1 more (map truncated)
  IfcType = 154
  LouvreSpacing = 0
  LouvreWidth = 0
  MoveBase = false
  MoveWithHost = true
  Normal = (0,0,0)
  Opening = 0
  OverallHeight = 3000
  OverallWidth = 895
  PartitioningType = 0
  PerimeterLength = 0
  Placement = pos=(24250,15110,0) rot=(0,0,-1;1.5708rad)
  PredefinedType = 0
  Preset = 0
  SymbolElevation = false
  SymbolPlan = false
  VerticalArea = 0
  Width = 895
  expr: OverallWidth = Width.Value
  expr: OverallHeight = Height.Value
FEATURE [Part::FeaturePython] Window038  label="Window 89x300 002"  # Arch/BIM 154 (typed FeaturePython)
  Area = 2685000
  CloneOf = -> Window033
  Frame = 0
  Height = 3000
  HoleDepth = 0
  HoleWire = 0
  HorizontalArea = 0
  IfcData = IfcUID=0OUFhGRqaHwRzx093rt3ko,+1 more (map truncated)
  IfcType = 154
  LouvreSpacing = 0
  LouvreWidth = 0
  MoveBase = false
  MoveWithHost = true
  Normal = (0,0,0)
  Opening = 0
  OverallHeight = 3000
  OverallWidth = 895
  PartitioningType = 0
  PerimeterLength = 0
  Placement = pos=(24250,14215,0) rot=(0,0,-1;1.5708rad)
  PredefinedType = 0
  Preset = 0
  SymbolElevation = false
  SymbolPlan = false
  VerticalArea = 0
  Width = 895
  expr: OverallWidth = Width.Value
  expr: OverallHeight = Height.Value
FEATURE [Part::FeaturePython] Window039  label="Window 89x300 001"  # Arch/BIM 154 (typed FeaturePython)
  Area = 2685000
  CloneOf = -> Window033
  Frame = 0
  Height = 3000
  HoleDepth = 0
  HoleWire = 0
  HorizontalArea = 0
  IfcData = IfcUID=0OUMhORqaHwRzx093rt3ko,+1 more (map truncated)
  IfcType = 154
  LouvreSpacing = 0
  LouvreWidth = 0
  MoveBase = false
  MoveWithHost = true
  Normal = (0,0,0)
  Opening = 0
  OverallHeight = 3000
  OverallWidth = 895
  PartitioningType = 0
  PerimeterLength = 0
  Placement = pos=(24250,16900,0) rot=(0,0,-1;1.5708rad)
  PredefinedType = 0
  Preset = 0
  SymbolElevation = false
  SymbolPlan = false
  VerticalArea = 0
  Width = 895
  expr: OverallWidth = Width.Value
  expr: OverallHeight = Height.Value
FEATURE [Part::FeaturePython] Window040  label="Window 89x300 "  # Arch/BIM 154 (typed FeaturePython)
  Area = 2685000
  CloneOf = -> Window033
  Frame = 0
  Height = 3000
  HoleDepth = 0
  HoleWire = 0
  HorizontalArea = 0
  IfcData = IfcUID=0OUThWRqaHwRzx093rt3ko,+1 more (map truncated)
  IfcType = 154
  LouvreSpacing = 0
  LouvreWidth = 0
  MoveBase = false
  MoveWithHost = true
  Normal = (0,0,0)
  Opening = 0
  OverallHeight = 3000
  OverallWidth = 895
  PartitioningType = 0
  PerimeterLength = 0
  Placement = pos=(24250,16005,0) rot=(0,0,-1;1.5708rad)
  PredefinedType = 0
  Preset = 0
  SymbolElevation = false
  SymbolPlan = false
  VerticalArea = 0
  Width = 895
  expr: OverallWidth = Width.Value
  expr: OverallHeight = Height.Value
FEATURE [Part::Part2DObjectPython] Wire002  # Draft 2D object (typed FeaturePython)
  ChamferSize = 0
  Closed = true
  End = (2920,-2017.5,0)
  FilletRadius = 0
  Length = 640
  MakeFace = true
  Placement = pos=(200,-200,0) rot=(0,0,1;0rad)
  Points = (12) [(2720,-1782.5,0),(2782.5,-1782.5,0),(2782.5,-1720,0),(2817.5,-1720,0),(2817.5,-1782.5,0),(2880,-1782.5,0),(2880,-1817.5,0),(2817.5,-1817.5,0),+4 more]
  Start = (2920,-1982.5,0)
  Subdivisions = 0
FEATURE [Part::FeaturePython] Structure  label="Column001"  # Arch/BIM 24 (typed FeaturePython)
  Base = -> Wire002
  FaceMaker = 0
  Height = 3000
  HorizontalArea = 9975
  IfcData = IfcUID=0OjUJ_RqaHwRzx093rt3ko,+1 more (map truncated)
  IfcType = 24
  Length = 0
  MoveBase = false
  MoveWithHost = true
  Nodes = (2) [(3000,-2000,0),(3000,-2000,3000)]
  NodesOffset = 0
  Normal = (0,0,1)
  PerimeterLength = 640
  PredefinedType = 0
  VerticalArea = 1.92e+06
  Width = 200
FEATURE [Part::FeaturePython] Structure001  label="Column005"  # Arch/BIM 24 (typed FeaturePython)
  CloneOf = -> Structure
  FaceMaker = 0
  Height = 3000
  HorizontalArea = 9975
  IfcData = IfcUID=0OjlcsRqaHwRzx093rt3ko,+1 more (map truncated)
  IfcType = 24
  Length = 0
  MoveBase = false
  MoveWithHost = true
  Nodes = (2) [(3000,-2000,0),(3000,-2000,3000)]
  NodesOffset = 0
  Normal = (0,0,0)
  PerimeterLength = 640
  Placement = pos=(-4.55e-13,-7000,0) rot=(0,0,1;0rad)
  PredefinedType = 0
  VerticalArea = 1.92e+06
  Width = 200
FEATURE [Part::FeaturePython] Structure002  label="Column002"  # Arch/BIM 24 (typed FeaturePython)
  CloneOf = -> Structure
  FaceMaker = 0
  Height = 3000
  HorizontalArea = 9975
  IfcData = IfcUID=0Ojrx4RqaHwRzx093rt3ko,+1 more (map truncated)
  IfcType = 24
  Length = 0
  MoveBase = false
  MoveWithHost = true
  Nodes = (2) [(3000,-2000,0),(3000,-2000,3000)]
  NodesOffset = 0
  Normal = (0,0,0)
  PerimeterLength = 640
  Placement = pos=(6333.33,-9.0495e-11,0) rot=(0,0,1;0rad)
  PredefinedType = 0
  VerticalArea = 1.92e+06
  Width = 200
FEATURE [Part::FeaturePython] Structure003  label="Column007"  # Arch/BIM 24 (typed FeaturePython)
  CloneOf = -> Structure
  FaceMaker = 0
  Height = 3000
  HorizontalArea = 9975
  IfcData = IfcUID=0Oj$bCRqaHwRzx093rt3ko,+1 more (map truncated)
  IfcType = 24
  Length = 0
  MoveBase = false
  MoveWithHost = true
  Nodes = (2) [(3000,-2000,0),(3000,-2000,3000)]
  NodesOffset = 0
  Normal = (0,0,0)
  PerimeterLength = 640
  Placement = pos=(6333.33,-7000,0) rot=(0,0,1;0rad)
  PredefinedType = 0
  VerticalArea = 1.92e+06
  Width = 200
FEATURE [Part::FeaturePython] Structure004  label="Column004"  # Arch/BIM 24 (typed FeaturePython)
  CloneOf = -> Structure
  FaceMaker = 0
  Height = 3000
  HorizontalArea = 9975
  IfcData = IfcUID=0Ok8ieRqaHwRzx093rt3ko,+1 more (map truncated)
  IfcType = 24
  Length = 0
  MoveBase = false
  MoveWithHost = true
  Nodes = (2) [(3000,-2000,0),(3000,-2000,3000)]
  NodesOffset = 0
  Normal = (0,0,0)
  PerimeterLength = 640
  Placement = pos=(12666.7,-8.95852e-11,0) rot=(0,0,1;0rad)
  PredefinedType = 0
  VerticalArea = 1.92e+06
  Width = 200
FEATURE [Part::FeaturePython] Structure005  label="Column006"  # Arch/BIM 24 (typed FeaturePython)
  CloneOf = -> Structure
  FaceMaker = 0
  Height = 3000
  HorizontalArea = 9975
  IfcData = IfcUID=0OkGiCRqaHwRzx093rt3ko,+1 more (map truncated)
  IfcType = 24
  Length = 0
  MoveBase = false
  MoveWithHost = true
  Nodes = (2) [(3000,-2000,0),(3000,-2000,3000)]
  NodesOffset = 0
  Normal = (0,0,0)
  PerimeterLength = 640
  Placement = pos=(12666.7,-7000,0) rot=(0,0,1;0rad)
  PredefinedType = 0
  VerticalArea = 1.92e+06
  Width = 200
FEATURE [Part::FeaturePython] Structure006  label="Column003"  # Arch/BIM 24 (typed FeaturePython)
  CloneOf = -> Structure
  FaceMaker = 0
  Height = 3000
  HorizontalArea = 9975
  IfcData = IfcUID=0OkOI8RqaHwRzx093rt3ko,+1 more (map truncated)
  IfcType = 24
  Length = 0
  MoveBase = false
  MoveWithHost = true
  Nodes = (2) [(3000,-2000,0),(3000,-2000,3000)]
  NodesOffset = 0
  Normal = (0,0,0)
  PerimeterLength = 640
  Placement = pos=(19000,4.55e-13,0) rot=(0,0,1;0rad)
  PredefinedType = 0
  VerticalArea = 1.92e+06
  Width = 200
FEATURE [Part::FeaturePython] Structure007  label="Column"  # Arch/BIM 24 (typed FeaturePython)
  CloneOf = -> Structure
  FaceMaker = 0
  Height = 3000
  HorizontalArea = 9975
  IfcData = IfcUID=0OkW1IRqaHwRzx093rt3ko,+1 more (map truncated)
  IfcType = 24
  Length = 0
  MoveBase = false
  MoveWithHost = true
  Nodes = (2) [(3000,-2000,0),(3000,-2000,3000)]
  NodesOffset = 0
  Normal = (0,0,0)
  PerimeterLength = 640
  Placement = pos=(19000,-7000,0) rot=(0,0,1;0rad)
  PredefinedType = 0
  VerticalArea = 1.92e+06
  Width = 200
FEATURE [Part::Part2DObjectPython] Rectangle003  # Draft 2D object (typed FeaturePython)
  Area = 299000000
  ChamferSize = 0
  Columns = 1
  FilletRadius = 0
  Height = 13000
  Length = 23000
  MakeFace = true
  Placement = pos=(24000,-12000,3000) rot=(0,1,0;3.14159rad)
  Rows = 1
FEATURE [Part::Part2DObjectPython] Wire003  # Draft 2D object (typed FeaturePython)
  Area = 8.836e+07
  ChamferSize = 0
  Closed = true
  End = (-22700,-2700,3000)
  FilletRadius = 0
  Length = 37600
  MakeFace = true
  Points = (4) [(-22700,6700,3000),(-13300,6700,3000),(-13300,-2700,3000),(-22700,-2700,3000)]
  Start = (-22700,6700,3000)
  Subdivisions = 0
FEATURE [Part::Part2DObjectPython] Rectangle004  # Draft 2D object (typed FeaturePython)
  ChamferSize = 0
  Columns = 1
  FilletRadius = 0
  Height = 9200
  Length = 9200
  MakeFace = true
  Placement = pos=(-13400,-2600,3200) rot=(0,1,0;3.14159rad)
  Rows = 1
FEATURE [Part::Part2DObjectPython] Rectangle005  # Draft 2D object (typed FeaturePython)
  ChamferSize = 0
  Columns = 1
  FilletRadius = 0
  Height = 12900
  Length = 22900
  MakeFace = true
  Placement = pos=(23950,-11950,3200) rot=(0,1,0;3.14159rad)
  Rows = 1
FEATURE [Part::FeaturePython] Structure010  # Arch/BIM 0 (typed FeaturePython)
  Base = -> Rectangle004
  FaceMaker = 0
  Height = 100
  HorizontalArea = 8.464e+07
  IfcType = 0
  Length = 0
  MoveBase = false
  MoveWithHost = true
  Nodes = (2) [(18000,2000,-3200),(18000,2000,-3100)]
  NodesOffset = 0
  Normal = (0,0,1)
  PerimeterLength = 36800
  VerticalArea = 3.68e+06
  Width = 200
FEATURE [Part::FeaturePython] Structure011  # Arch/BIM 0 (typed FeaturePython)
  Base = -> Rectangle005
  FaceMaker = 0
  Height = 100
  HorizontalArea = 2.9541e+08
  IfcType = 0
  Length = 0
  MoveBase = false
  MoveWithHost = true
  Nodes = (2) [(-12500,-5500,-3200),(-12500,-5500,-3100)]
  NodesOffset = 0
  Normal = (0,0,1)
  PerimeterLength = 71600
  VerticalArea = 7.16e+06
  Width = 200
FEATURE [Part::Fillet] Fillet
  Base = -> Structure010
  Edges = 4 edges r=50: [Edge4,Edge7,Edge10,Edge12]
FEATURE [Part::Fillet] Fillet001
  Base = -> Structure011
  Edges = 4 edges r=50: [Edge4,Edge7,Edge10,Edge12]
FEATURE [App::DocumentObjectGroup] Group007  label="Columns"
  Group = -> [Structure,Structure001,Structure002,Structure003,Structure004,Structure005,Structure006,Structure007]
FEATURE [App::DocumentObjectGroup] Group009  label="Fixed windows 300 high"
  Group = -> [Window033,Window034,Window035,Window036,Window037,Window038,Window039,Window040,Window032,Window029,Window028,Window027,Window026,Window025,Window022,Window024,Window023,Window021,Window020,Window019,Window018,Window017,Window016,Window015,Window014,Window013,Window012,Window007,Window008,Window009,Window010]
FEATURE [App::DocumentObjectGroup] Group010  label="Fixed windows 90 high"
  Group = -> [Window031,Window030,Window011]
FEATURE [App::DocumentObjectGroup] Group011  label="Glass doors 210 high"
  Group = -> [Window004,Window005,Window006]
FEATURE [App::DocumentObjectGroup] Group008  label="Windows"
  Group = -> [Group009,Group010,Group011,Window]
FEATURE [App::DocumentObjectGroup] Group012  label="Doors"
  Group = -> [Window002,Window001,Window003]
FEATURE [App::DocumentObjectGroup] Group014  label="Exterior walls 16cm"
  Group = -> [Wall001,Wall,Wall002,Wall003,Wall004]
FEATURE [App::DocumentObjectGroup] Group015  label="Interior walls 10cm"
  Group = -> [Wall005,Wall006,Wall007]
FEATURE [App::DocumentObjectGroup] Group013  label="Walls"
  Group = -> [Group014,Group015]
FEATURE [App::DocumentObjectGroup] Group016  label="Original 2D drawings"
  Group = -> [Group,Group001,Group002,Group003,Group004,Group005]
FEATURE [Part::Part2DObjectPython] Rectangle006  # Draft 2D object (typed FeaturePython)
  ChamferSize = 0
  Columns = 1
  FilletRadius = 0
  Height = 1000
  Length = 1000
  MakeFace = false
  Placement = pos=(-23000,-16000,0) rot=(0,0,1;0rad)
  Rows = 1
FEATURE [Part::Offset2D] Offset2D
  Fill = false
  Intersection = false
  Join = 0
  Mode = 1
  SelfIntersection = false
  Source = -> Rectangle006
  Value = -5
FEATURE [Part::FeaturePython] Structure012  label="Floor element"  # Arch/BIM 0 (typed FeaturePython)
  Base = -> Offset2D
  FaceMaker = 0
  Height = 100
  HorizontalArea = 980100
  IfcType = 0
  Length = 0
  MoveBase = false
  MoveWithHost = false
  Nodes = (2) [(-22500,-15500,0),(-22500,-15500,-100)]
  NodesOffset = 0
  Normal = (0,0,-1)
  PerimeterLength = 3960
  VerticalArea = 396000
  Width = 200
FEATURE [Part::FeaturePython] Structure013  label="Floor elements"  # Arch/BIM 0 (typed FeaturePython)
  CloneOf = -> Structure012
  FaceMaker = 0
  Height = 100
  HorizontalArea = 980100
  IfcData = IfcUID=0M4F1eRqaHwRzx093rt3ko
  IfcType = 0
  Length = 0
  MoveBase = false
  MoveWithHost = true
  Nodes = (2) [(-22500,-15500,0),(-22500,-15500,-100)]
  NodesOffset = 0
  Normal = (0,0,0)
  PerimeterLength = 3960
  Placement = pos=(0,1000,0) rot=(0,0,1;0rad)
  VerticalArea = 396000
  Width = 200
FEATURE [Part::FeaturePython] Array  label="Floor elements001"  # Draft array (typed FeaturePython)
  Angle = 360
  ArrayType = 0
  Axis = (0,0,1)
  Base = -> Structure012
  Center = (0,0,0)
  Fuse = false
  IntervalAxis = (0,0,0)
  IntervalX = (1000,0,0)
  IntervalY = (0,1,0)
  IntervalZ = (0,0,1)
  NumberPolar = 1
  NumberX = 39
  NumberY = 1
  NumberZ = 1
FEATURE [Part::FeaturePython] Array001  label="Floor elements002"  # Draft array (typed FeaturePython)
  Angle = 360
  ArrayType = 0
  Axis = (0,0,1)
  Base = -> Structure012
  Center = (0,0,0)
  Fuse = false
  IntervalAxis = (0,0,0)
  IntervalX = (1000,0,0)
  IntervalY = (0,1000,0)
  IntervalZ = (0,0,1)
  NumberPolar = 1
  NumberX = 15
  NumberY = 3
  NumberZ = 1
  Placement = pos=(21000,1000,0) rot=(0,0,1;0rad)
FEATURE [Part::FeaturePython] Array002  label="Floor elements003"  # Draft array (typed FeaturePython)
  Angle = 360
  ArrayType = 0
  Axis = (0,0,1)
  Base = -> Structure012
  Center = (0,0,0)
  Fuse = false
  IntervalAxis = (0,0,0)
  IntervalX = (1000,0,0)
  IntervalY = (0,1,0)
  IntervalZ = (0,0,1)
  NumberPolar = 1
  NumberX = 31
  NumberY = 1
  NumberZ = 1
  Placement = pos=(21000,4000,0) rot=(0,0,1;0rad)
FEATURE [Part::FeaturePython] Structure014  label="Floor elements004"  # Arch/BIM 0 (typed FeaturePython)
  CloneOf = -> Structure012
  FaceMaker = 0
  Height = 100
  HorizontalArea = 980100
  IfcData = IfcUID=0MYA$WRqaHwRzx093rt3ko
  IfcType = 0
  Length = 0
  MoveBase = false
  MoveWithHost = true
  Nodes = (2) [(-22500,-15500,0),(-22500,-15500,-100)]
  NodesOffset = 0
  Normal = (0,0,0)
  PerimeterLength = 3960
  Placement = pos=(51000,5000,0) rot=(0,0,1;0rad)
  VerticalArea = 396000
  Width = 200
FEATURE [Part::FeaturePython] Array003  label="Floor elements005"  # Draft array (typed FeaturePython)
  Angle = 360
  ArrayType = 0
  Axis = (0,0,1)
  Base = -> Structure012
  Center = (0,0,0)
  Fuse = false
  IntervalAxis = (0,0,0)
  IntervalX = (1000,0,0)
  IntervalY = (0,1000,0)
  IntervalZ = (0,0,1)
  NumberPolar = 1
  NumberX = 26
  NumberY = 5
  NumberZ = 1
  Placement = pos=(21000,5000,0) rot=(0,0,1;0rad)
FEATURE [Part::FeaturePython] Array004  label="Floor elements006"  # Draft array (typed FeaturePython)
  Angle = 360
  ArrayType = 0
  Axis = (0,0,1)
  Base = -> Structure012
  Center = (0,0,0)
  Fuse = false
  IntervalAxis = (0,0,0)
  IntervalX = (1000,0,0)
  IntervalY = (0,1000,0)
  IntervalZ = (0,0,1)
  NumberPolar = 1
  NumberX = 46
  NumberY = 7
  NumberZ = 1
  Placement = pos=(1000,10000,0) rot=(0,0,1;0rad)
FEATURE [Part::FeaturePython] Array005  label="Floor elements007"  # Draft array (typed FeaturePython)
  Angle = 360
  ArrayType = 0
  Axis = (0,0,1)
  Base = -> Structure012
  Center = (0,0,0)
  Fuse = false
  IntervalAxis = (0,0,0)
  IntervalX = (1000,0,0)
  IntervalY = (0,1000,0)
  IntervalZ = (0,0,1)
  NumberPolar = 1
  NumberX = 8
  NumberY = 5
  NumberZ = 1
  Placement = pos=(1000,17000,0) rot=(0,0,1;0rad)
FEATURE [App::DocumentObjectGroup] Group017  label="Flooring"
  Group = -> [Structure013,Array,Array001,Array002,Structure014,Array003,Array004,Array005]
FEATURE [Part::Part2DObjectPython] Rectangle007  # Draft 2D object (typed FeaturePython)
  ChamferSize = 0
  Columns = 1
  FilletRadius = 0
  Height = 300
  Length = 300
  MakeFace = true
  Placement = pos=(-15100,-1650,0) rot=(0,0,1;0rad)
  Rows = 1
FEATURE [Part::FeaturePython] Structure015  label="Bench support"  # Arch/BIM 0 (typed FeaturePython)
  Base = -> Rectangle007
  FaceMaker = 0
  Height = 400
  HorizontalArea = 90000
  IfcData = IfcUID=0M2zfMRqaHwRzx093rt3ko
  IfcType = 0
  Length = 0
  MoveBase = false
  MoveWithHost = true
  Nodes = (2) [(-14950,-1500,0),(-14950,-1500,400)]
  NodesOffset = 0
  Normal = (0,0,0)
  PerimeterLength = 1200
  VerticalArea = 480000
  Width = 200
FEATURE [Part::FeaturePython] Structure016  label="Bench support007"  # Arch/BIM 0 (typed FeaturePython)
  CloneOf = -> Structure015
  FaceMaker = 0
  Height = 400
  HorizontalArea = 90000
  IfcData = IfcUID=0M3BbsRqaHwRzx093rt3ko
  IfcType = 0
  Length = 0
  MoveBase = false
  MoveWithHost = true
  Nodes = (2) [(-14950,-1500,0),(-14950,-1500,400)]
  NodesOffset = 0
  Normal = (0,0,0)
  PerimeterLength = 1200
  Placement = pos=(2150,-3.16049e-11,0) rot=(0,0,1;0rad)
  VerticalArea = 480000
  Width = 200
FEATURE [Part::FeaturePython] Structure017  label="Bench support006"  # Arch/BIM 0 (typed FeaturePython)
  CloneOf = -> Structure015
  FaceMaker = 0
  Height = 400
  HorizontalArea = 90000
  IfcData = IfcUID=0M3HxARqaHwRzx093rt3ko
  IfcType = 0
  Length = 0
  MoveBase = false
  MoveWithHost = true
  Nodes = (2) [(-14950,-1500,0),(-14950,-1500,400)]
  NodesOffset = 0
  Normal = (0,0,0)
  PerimeterLength = 1200
  Placement = pos=(4270,9.09e-13,0) rot=(0,0,1;0rad)
  VerticalArea = 480000
  Width = 200
FEATURE [Part::FeaturePython] Structure018  label="Bench support002"  # Arch/BIM 0 (typed FeaturePython)
  CloneOf = -> Structure015
  FaceMaker = 0
  Height = 400
  HorizontalArea = 90000
  IfcData = IfcUID=0M3O9IRqaHwRzx093rt3ko
  IfcType = 0
  Length = 0
  MoveBase = false
  MoveWithHost = true
  Nodes = (2) [(-14950,-1500,0),(-14950,-1500,400)]
  NodesOffset = 0
  Normal = (0,0,0)
  PerimeterLength = 1200
  Placement = pos=(6390,4.55e-13,0) rot=(0,0,1;0rad)
  VerticalArea = 480000
  Width = 200
FEATURE [Part::FeaturePython] Structure019  label="Bench support004"  # Arch/BIM 0 (typed FeaturePython)
  CloneOf = -> Structure015
  FaceMaker = 0
  Height = 400
  HorizontalArea = 90000
  IfcData = IfcUID=0M3VHERqaHwRzx093rt3ko
  IfcType = 0
  Length = 0
  MoveBase = false
  MoveWithHost = true
  Nodes = (2) [(-14950,-1500,0),(-14950,-1500,400)]
  NodesOffset = 0
  Normal = (0,0,0)
  PerimeterLength = 1200
  Placement = pos=(12750,6.23e-11,0) rot=(0,0,1;0rad)
  VerticalArea = 480000
  Width = 200
FEATURE [Part::FeaturePython] Structure020  label="Bench support001"  # Arch/BIM 0 (typed FeaturePython)
  CloneOf = -> Structure015
  FaceMaker = 0
  Height = 400
  HorizontalArea = 90000
  IfcData = IfcUID=0M3fCORqaHwRzx093rt3ko
  IfcType = 0
  Length = 0
  MoveBase = false
  MoveWithHost = true
  Nodes = (2) [(-14950,-1500,0),(-14950,-1500,400)]
  NodesOffset = 0
  Normal = (0,0,0)
  PerimeterLength = 1200
  Placement = pos=(10630,6.27551e-11,0) rot=(0,0,1;0rad)
  VerticalArea = 480000
  Width = 200
FEATURE [Part::FeaturePython] Structure021  label="Bench support005"  # Arch/BIM 0 (typed FeaturePython)
  CloneOf = -> Structure015
  FaceMaker = 0
  Height = 400
  HorizontalArea = 90000
  IfcData = IfcUID=0M3nEIRqaHwRzx093rt3ko
  IfcType = 0
  Length = 0
  MoveBase = false
  MoveWithHost = true
  Nodes = (2) [(-14950,-1500,0),(-14950,-1500,400)]
  NodesOffset = 0
  Normal = (0,0,0)
  PerimeterLength = 1200
  Placement = pos=(8510,3.0241e-11,0) rot=(0,0,1;0rad)
  VerticalArea = 480000
  Width = 200
FEATURE [Part::FeaturePython] Structure022  label="Bench support003"  # Arch/BIM 0 (typed FeaturePython)
  CloneOf = -> Structure015
  FaceMaker = 0
  Height = 400
  HorizontalArea = 90000
  IfcData = IfcUID=0M3upwRqaHwRzx093rt3ko
  IfcType = 0
  Length = 0
  MoveBase = false
  MoveWithHost = true
  Nodes = (2) [(-14950,-1500,0),(-14950,-1500,400)]
  NodesOffset = 0
  Normal = (0,0,0)
  PerimeterLength = 1200
  Placement = pos=(14900,1.1369e-12,0) rot=(0,0,1;0rad)
  VerticalArea = 480000
  Width = 200
FEATURE [Part::Part2DObjectPython] Rectangle008  # Draft 2D object (typed FeaturePython)
  ChamferSize = 0
  Columns = 1
  FilletRadius = 0
  Height = 500
  Length = 15400
  MakeFace = true
  Placement = pos=(-15200,-1750,400) rot=(0,0,1;0rad)
  Rows = 1
FEATURE [Part::FeaturePython] Structure023  label="Bench table"  # Arch/BIM 0 (typed FeaturePython)
  Base = -> Rectangle008
  FaceMaker = 0
  Height = 100
  HorizontalArea = 7.7e+06
  IfcData = IfcUID=0M40NCRqaHwRzx093rt3ko
  IfcType = 0
  Length = 0
  MoveBase = false
  MoveWithHost = true
  Nodes = (2) [(-7500,-1500,400),(-7500,-1500,500)]
  NodesOffset = 0
  Normal = (0,0,0)
  PerimeterLength = 31800
  VerticalArea = 3.18e+06
  Width = 200
FEATURE [App::DocumentObjectGroup] Group018  label="Bench"
  Group = -> [Structure015,Structure016,Structure017,Structure018,Structure019,Structure020,Structure021,Structure022,Structure023]
FEATURE [Part::Part2DObjectPython] Wire004  # Draft 2D object (typed FeaturePython)
  ChamferSize = 0
  Closed = true
  End = (8500,-24500,3300)
  FilletRadius = 0
  Length = 14704.5
  MakeFace = true
  Placement = pos=(1150,-24500,3300) rot=(1,0,0;1.5708rad)
  Points = (3) [(0,0,0),(1350,-100,0),(7350,-6.36646e-12,0)]
  Start = (1150,-24500,3300)
  Subdivisions = 0
FEATURE [Part::Part2DObjectPython] Wire005  # Draft 2D object (typed FeaturePython)
  ChamferSize = 0
  Closed = true
  End = (23850,-24500,3300)
  FilletRadius = 0
  Length = 30701.5
  MakeFace = true
  Placement = pos=(8500,-24500,3300) rot=(1,0,0;1.5708rad)
  Points = (3) [(0,0,0),(10500,-100,0),(15350,1.36424e-12,0)]
  Start = (8500,-24500,3300)
  Subdivisions = 0
FEATURE [Part::Part2DObjectPython] Wire006  # Draft 2D object (typed FeaturePython)
  ChamferSize = 0
  Closed = true
  End = (39966.7,-5500,3300)
  FilletRadius = 0
  Length = 12707.4
  MakeFace = true
  Placement = pos=(39966.7,-11850,3300) rot=(0.57735,-0.57735,-0.57735;2.0944rad)
  Points = (3) [(0,0,0),(-770,-100,0),(-6350,6.54836e-11,0)]
  Start = (39966.7,-11850,3300)
  Subdivisions = 0
FEATURE [Part::Part2DObjectPython] Wire007  # Draft 2D object (typed FeaturePython)
  ChamferSize = 0
  Closed = true
  End = (39966.7,850,3300)
  FilletRadius = 0
  Length = 12707.4
  MakeFace = true
  Placement = pos=(39966.7,-5500,3300) rot=(0.57735,-0.57735,-0.57735;2.0944rad)
  Points = (3) [(0,0,0),(-5580,-100,0),(-6350,0,0)]
  Start = (39966.7,-5500,3300)
  Subdivisions = 0
FEATURE [Part::FeaturePython] Structure024  label="Structure"  # Arch/BIM 0 (typed FeaturePython)
  Base = -> Wire005
  FaceMaker = 0
  Height = 30000
  HorizontalArea = 460500000
  IfcType = 0
  Length = 0
  MoveBase = false
  MoveWithHost = true
  Nodes = (2) [(17116.7,-24466.7,3233.33),(17116.7,-24466.7,-26766.7)]
  NodesOffset = 0
  Normal = (0,1,0)
  PerimeterLength = 90700
  VerticalArea = 1.535e+06
  Width = 200
FEATURE [Part::FeaturePython] Structure025  label="Structure012"  # Arch/BIM 0 (typed FeaturePython)
  Base = -> Wire004
  FaceMaker = 0
  Height = 30000
  HorizontalArea = 2.205e+08
  IfcType = 0
  Length = 0
  MoveBase = false
  MoveWithHost = true
  Nodes = (2) [(4050,-24466.7,3233.33),(4050,-24466.7,-26766.7)]
  NodesOffset = 0
  Normal = (0,1,0)
  PerimeterLength = 74700
  VerticalArea = 735000
  Width = 200
FEATURE [Part::FeaturePython] Structure026  label="Structure013"  # Arch/BIM 0 (typed FeaturePython)
  Base = -> Wire007
  FaceMaker = 0
  Height = 100000
  HorizontalArea = 6.35e+08
  IfcType = 0
  Length = 0
  MoveBase = false
  MoveWithHost = true
  Nodes = (2) [(1523.33,-43943.4,-7243.33),(1523.33,-43943.4,-107243)]
  NodesOffset = 0
  Normal = (-1,0,0)
  PerimeterLength = 212700
  VerticalArea = 635000
  Width = 200
FEATURE [Part::FeaturePython] Structure027  label="Structure014"  # Arch/BIM 0 (typed FeaturePython)
  Base = -> Wire006
  FaceMaker = 0
  Height = 100000
  HorizontalArea = 6.35e+08
  IfcType = 0
  Length = 0
  MoveBase = false
  MoveWithHost = true
  Nodes = (2) [(9476.67,-42340,-5640),(9476.67,-42340,-105640)]
  NodesOffset = 0
  Normal = (-1,0,0)
  PerimeterLength = 212700
  VerticalArea = 635000
  Width = 200
FEATURE [Part::MultiCommon] Common
  Refine = true
  Shapes = -> [Structure025,Structure027]
FEATURE [Part::MultiCommon] Common001
  Refine = true
  Shapes = -> [Structure026,Structure024]
FEATURE [Part::MultiCommon] Common002
  Refine = true
  Shapes = -> [Structure026,Structure025]
FEATURE [Part::MultiCommon] Common003
  Refine = true
  Shapes = -> [Structure027,Structure024]
FEATURE [Part::FeaturePython] Structure008  label="Roof slab001"  # Arch/BIM 110 (typed FeaturePython)
  Additions = -> [Fillet001]
  Base = -> Rectangle003
  FaceMaker = 0
  Height = 200
  HorizontalArea = 295430000
  IfcData = IfcUID=0Qfz_IRqaHwRzx093rt3ko,+1 more (map truncated)
  IfcType = 110
  Length = 0
  MoveBase = false
  MoveWithHost = true
  Nodes = (4) [(-1000,-12000,-3000),(-24000,-12000,-3000),(-24000,1000,-3000),(-1000,1000,-3000)]
  NodesOffset = 0
  Normal = (0,0,1)
  PerimeterLength = 72000
  PredefinedType = 0
  Subtractions = -> [Common003,Common002,Common001,Common]
  VerticalArea = 2.3592e+07
  Width = 200
FEATURE [Part::Part2DObjectPython] Wire008  # Draft 2D object (typed FeaturePython)
  ChamferSize = 0
  Closed = true
  End = (-18000,-24500,3300)
  FilletRadius = 0
  Length = 9210.75
  MakeFace = true
  Placement = pos=(-22600,-24500,3300) rot=(1,0,0;1.5708rad)
  Points = (3) [(0,0,0),(520,-100,0),(4600,-1.36424e-12,0)]
  Start = (-22600,-24500,3300)
  Subdivisions = 0
FEATURE [Part::Part2DObjectPython] Wire009  # Draft 2D object (typed FeaturePython)
  ChamferSize = 0
  Closed = true
  End = (-13400,-24500,3300)
  FilletRadius = 0
  Length = 9204.41
  MakeFace = true
  Placement = pos=(-18000,-24500,3300) rot=(1,0,0;1.5708rad)
  Points = (3) [(0,0,0),(2580,-100,0),(4600,9.45874e-11,0)]
  Start = (-18000,-24500,3300)
  Subdivisions = 0
FEATURE [Part::Part2DObjectPython] Wire010  # Draft 2D object (typed FeaturePython)
  ChamferSize = 0
  Closed = true
  End = (-31600,-2600,3300)
  FilletRadius = 0
  Length = 18402.7
  MakeFace = true
  Placement = pos=(-31600,6600,3300) rot=(0.57735,-0.57735,-0.57735;2.0944rad)
  Points = (3) [(0,0,0),(6600,-100,0),(9200,-3.63798e-12,0)]
  Start = (-31600,6600,3300)
  Subdivisions = 0
FEATURE [Part::FeaturePython] Structure028  label="Structure015"  # Arch/BIM 0 (typed FeaturePython)
  Base = -> Wire010
  FaceMaker = 0
  Height = 20000
  HorizontalArea = 1.84e+08
  IfcType = 0
  Length = 0
  MoveBase = false
  MoveWithHost = true
  Nodes = (2) [(1333.33,36866.7,8533.33),(1333.33,36866.7,-11466.7)]
  NodesOffset = 0
  Normal = (1,0,0)
  PerimeterLength = 58400
  VerticalArea = 920000
  Width = 200
FEATURE [Part::FeaturePython] Structure029  label="Structure016"  # Arch/BIM 0 (typed FeaturePython)
  Base = -> Wire009
  FaceMaker = 0
  Height = 100000
  HorizontalArea = 4.6e+08
  IfcType = 0
  Length = 0
  MoveBase = false
  MoveWithHost = true
  Nodes = (2) [(-15606.7,-24466.7,3233.33),(-15606.7,-24466.7,-96766.7)]
  NodesOffset = 0
  Normal = (0,1,0)
  PerimeterLength = 209200
  VerticalArea = 460000
  Width = 200
FEATURE [Part::FeaturePython] Structure030  label="Structure017"  # Arch/BIM 0 (typed FeaturePython)
  Base = -> Wire008
  FaceMaker = 0
  Height = 100000
  HorizontalArea = 4.6e+08
  IfcType = 0
  Length = 0
  MoveBase = false
  MoveWithHost = true
  Nodes = (2) [(-20893.3,-24466.7,3233.33),(-20893.3,-24466.7,-96766.7)]
  NodesOffset = 0
  Normal = (0,1,0)
  PerimeterLength = 209200
  VerticalArea = 460000
  Width = 200
FEATURE [Part::MultiCommon] Common004
  Refine = true
  Shapes = -> [Structure028,Structure030]
FEATURE [Part::MultiCommon] Common005
  Refine = true
  Shapes = -> [Structure028,Structure029]
FEATURE [Part::FeaturePython] Structure009  label="Roof slab"  # Arch/BIM 110 (typed FeaturePython)
  Additions = -> [Fillet]
  Base = -> Wire003
  FaceMaker = 0
  Height = 200
  HorizontalArea = 8.653e+07
  IfcData = IfcUID=0OkeaoRqaHwRzx093rt3ko,+1 more (map truncated)
  IfcType = 110
  Length = 0
  MoveBase = false
  MoveWithHost = true
  Nodes = (4) [(-22700,6700,3000),(-13300,6700,3000),(-13300,-2700,3000),(-22700,-2700,3000)]
  NodesOffset = 0
  Normal = (0,0,1)
  PerimeterLength = 37600
  PredefinedType = 0
  Subtractions = -> [Common005,Common004]
  VerticalArea = 1.22388e+07
  Width = 200
FEATURE [App::DocumentObjectGroup] Group006  label="Roof slabs"
  Group = -> [Structure009,Structure008]
FEATURE [Part::Part2DObjectPython] Wire011  # Draft 2D object (typed FeaturePython)
  ChamferSize = 0
  Closed = false
  End = (-31600,-24500,-756.752)
  FilletRadius = 0
  Length = 39416.9
  MakeFace = true
  Placement = pos=(-31600,14800,1726.61) rot=(0.57735,-0.57735,-0.57735;2.0944rad)
  Points = (5) [(0,0,0),(6754.73,-339.576,0),(28800,-2526.61,0),(33499.6,-2526.61,0),(39300,-2483.36,0)]
  Start = (-31600,14800,1726.61)
  Subdivisions = 0
FEATURE [Part::Part2DObjectPython] Wire012  # Draft 2D object (typed FeaturePython)
  ChamferSize = 0
  Closed = false
  End = (39966.7,-24500,-1266.71)
  FilletRadius = 0
  Length = 71587.3
  MakeFace = true
  Placement = pos=(-31600,-24500,-756.752) rot=(1,0,0;1.5708rad)
  Points = (4) [(0,0,0),(5788.87,1.13687e-13,0),(65428,-917.525,0),(71566.7,-509.958,1.09139e-11)]
  Start = (-31600,-24500,-756.752)
  Subdivisions = 0
FEATURE [Part::Part2DObjectPython] Wire013  # Draft 2D object (typed FeaturePython)
  ChamferSize = 0
  Closed = false
  End = (39966.7,14800,-536.031)
  FilletRadius = 0
  Length = 39363.5
  MakeFace = true
  Placement = pos=(39966.7,-24500,-1266.71) rot=(0.57735,-0.57735,-0.57735;2.0944rad)
  Points = (6) [(0,0,0),(-6410.27,-4.09273e-12,0),(-14500,-4.04725e-11,0),(-24660,1066.71,0),(-31961.5,1066.71,0),(-39300,730.678,0)]
  Start = (39966.7,-24500,-1266.71)
  Subdivisions = 0
FEATURE [Part::Part2DObjectPython] Wire014  # Draft 2D object (typed FeaturePython)
  ChamferSize = 0
  Closed = false
  End = (-31600,14800,1726.61)
  FilletRadius = 0
  Length = 71710.6
  MakeFace = true
  Placement = pos=(39966.7,14800,-536.031) rot=(-1,0,0;1.5708rad)
  Points = (6) [(0,0,0),(-6138.74,0,0),(-23966.7,-436.031,-1.81899e-12),(-53806.7,-436.031,-1.81899e-12),(-65777.8,-2262.64,-1.81899e-12),+1 more]
  Start = (39966.7,14800,-536.031)
  Subdivisions = 0
FEATURE [Part::Part2DObjectPython] BSpline  # Draft 2D object (typed FeaturePython)
  Closed = false
  MakeFace = true
  Parameterization = 1
  Placement = pos=(-31600,14800,1726.61) rot=(0.57735,-0.57735,-0.57735;2.0944rad)
  Points = (5) [(0,0,0),(6754.73,-339.576,0),(28800,-2526.61,0),(33499.6,-2526.61,0),(39300,-2483.36,0)]
FEATURE [Part::Part2DObjectPython] BSpline001  # Draft 2D object (typed FeaturePython)
  Closed = false
  MakeFace = true
  Parameterization = 1
  Placement = pos=(-31600,-24500,-756.752) rot=(1,0,0;1.5708rad)
  Points = (4) [(0,0,0),(5788.87,1.13687e-13,0),(65428,-917.525,0),(71566.7,-509.958,1.09139e-11)]
FEATURE [Part::Part2DObjectPython] BSpline002  # Draft 2D object (typed FeaturePython)
  Closed = false
  MakeFace = true
  Parameterization = 1
  Placement = pos=(39966.7,-24500,-1266.71) rot=(0.57735,-0.57735,-0.57735;2.0944rad)
  Points = (6) [(0,0,0),(-6410.27,-4.09273e-12,0),(-14500,-4.04725e-11,0),(-24660,1066.71,0),(-31961.5,1066.71,0),(-39300,730.678,0)]
FEATURE [Part::Part2DObjectPython] BSpline003  # Draft 2D object (typed FeaturePython)
  Closed = false
  MakeFace = true
  Parameterization = 1
  Placement = pos=(39966.7,14800,-536.031) rot=(-1,0,0;1.5708rad)
  Points = (6) [(0,0,0),(-6138.74,0,0),(-23966.7,-436.031,-1.81899e-12),(-53806.7,-436.031,-1.81899e-12),(-65777.8,-2262.64,-1.81899e-12),+1 more]
FEATURE [Surface::GeomFillSurface] Surface
  BoundaryList = -> [BSpline,BSpline001,BSpline002,BSpline003]
  FillType = 0
FEATURE [Part::Part2DObjectPython] Wire015  # Draft 2D object (typed FeaturePython)
  ChamferSize = 0
  Closed = true
  End = (16000,-16000,2200)
  FilletRadius = 0
  Length = 148720
  MakeFace = true
  Placement = pos=(-23000,-16000,2200) rot=(0,0,1;0rad)
  Points = (16) [(0,0,0),(0,2000,0),(840,2000,0),(840,22160,0),(9160,22160,0),(9160,17000,0),(46950,17000,0),(46950,16160,0),(51160,16160,0),(51160,6000,0),+6 more]
  Start = (-23000,-16000,2200)
  Subdivisions = 0
FEATURE [Part::FeaturePython] Structure031  label="Structure018"  # Arch/BIM 0 (typed FeaturePython)
  Base = -> Wire015
  FaceMaker = 0
  Height = 10000
  HorizontalArea = 8.48955e+08
  IfcType = 0
  Length = 0
  MoveBase = false
  MoveWithHost = true
  Nodes = (2) [(739.717,-6618.46,2200),(739.717,-6618.46,-7800)]
  NodesOffset = 0
  Normal = (0,0,0)
  PerimeterLength = 148720
  VerticalArea = 1.4872e+09
  Width = 200
FEATURE [Part::Cut] Cut  label="Terrain shape"
  Base = -> Surface
  Refine = true
  Tool = -> Structure031
FEATURE [App::DocumentObjectGroup] Group021  label="Terrain construction"
  Group = -> [Wire011,Wire012,Wire013,Wire014,BSpline,BSpline001,BSpline002,BSpline003]
FEATURE [App::DocumentObjectGroup] Group020  label="Construction geometry"
  Group = -> [Group021]
FEATURE [Part::Part2DObjectPython] Wire017  # Draft 2D object (typed FeaturePython)
  ChamferSize = 0
  Closed = false
  End = (23995,5,-100)
  FilletRadius = 0
  Length = 38990
  MakeFace = true
  Placement = pos=(-14005,995,-100) rot=(0.707107,0.707107,0;3.14159rad)
  Points = (3) [(0,0,0),(8.41283e-12,38000,0),(-990,38000,0)]
  Start = (-14005,995,-100)
  Subdivisions = 0
FEATURE [Part::FeaturePython] Wall009  label="Footing wall"  # Arch/BIM 150 (typed FeaturePython)
  Align = 1
  Base = -> Wire017
  BlockHeight = 0
  BlockLength = 1000
  CountBroken = 0
  CountEntire = 0
  Face = 0
  Height = 2000
  HorizontalArea = 6.2128e+06
  IfcData = IfcUID=0L$thCRqaHwRzx093rt3ko,+1 more (map truncated)
  IfcType = 150
  Joint = 0
  Length = 38990
  MakeBlocks = true
  MoveBase = false
  MoveWithHost = true
  Normal = (0,0,-1)
  OffsetFirst = 0
  OffsetSecond = 0
  PerimeterLength = 77980
  PredefinedType = 0
  VerticalArea = 155960000
  Width = 160
FEATURE [Part::Part2DObjectPython] Wire018  # Draft 2D object (typed FeaturePython)
  ChamferSize = 0
  Closed = false
  End = (-13840,995,0)
  FilletRadius = 0
  Length = 33645
  MakeFace = true
  Placement = pos=(-22160,-14000,0) rot=(0,1,0;3.14159rad)
  Points = (4) [(0,0,0),(0,20160,0),(-8320,20160,0),(-8320,14995,0)]
  Start = (-22160,-14000,0)
  Subdivisions = 0
  Support = -> [Wall]
FEATURE [Part::FeaturePython] Wall010  label="Footing wall001"  # Arch/BIM 150 (typed FeaturePython)
  Align = 1
  Base = -> Wire018
  BlockHeight = 0
  BlockLength = 0
  CountBroken = 0
  CountEntire = 0
  Face = 0
  Height = 2100
  HorizontalArea = 5.332e+06
  IfcData = IfcUID=0M0MzORqaHwRzx093rt3ko,+1 more (map truncated)
  IfcType = 150
  Joint = 0
  Length = 33645
  MakeBlocks = false
  MoveBase = false
  MoveWithHost = true
  Normal = (0,0,-1)
  OffsetFirst = 0
  OffsetSecond = 0
  PerimeterLength = 66970
  PredefinedType = 0
  VerticalArea = 1.40637e+08
  Width = 160
FEATURE [Part::Part2DObjectPython] Wire019  # Draft 2D object (typed FeaturePython)
  ChamferSize = 0
  Closed = false
  End = (23995,160,0)
  FilletRadius = 0
  Length = 14325
  MakeFace = true
  Placement = pos=(28160,-10000,0) rot=(0,1,0;3.14159rad)
  Points = (3) [(0,0,0),(-2.18279e-11,10160,0),(4165,10160,0)]
  Start = (28160,-10000,0)
  Subdivisions = 0
  Support = -> [Wall010]
FEATURE [Part::FeaturePython] Wall011  label="Footing wall002"  # Arch/BIM 150 (typed FeaturePython)
  Align = 0
  Base = -> Wire019
  BlockHeight = 0
  BlockLength = 0
  CountBroken = 0
  CountEntire = 0
  Face = 0
  Height = 2100
  HorizontalArea = 2.2664e+06
  IfcData = IfcUID=0M0sSORqaHwRzx093rt3ko,+1 more (map truncated)
  IfcType = 150
  Joint = 0
  Length = 14325
  MakeBlocks = false
  MoveBase = false
  MoveWithHost = true
  Normal = (0,0,-1)
  OffsetFirst = 0
  OffsetSecond = 0
  PerimeterLength = 28650
  PredefinedType = 0
  VerticalArea = 6.0165e+07
  Width = 160
FEATURE [Part::Part2DObjectPython] Wire020  # Draft 2D object (typed FeaturePython)
  ChamferSize = 0
  Closed = true
  End = (13000,-15000,-550.127)
  FilletRadius = 0
  Length = 8605.08
  MakeFace = true
  Placement = pos=(13000,-15000,-155.214) rot=(-1,0,0;1.5708rad)
  Points = (19) [(0,0,0),(350,-2.84217e-14,0),(350,155.214,0),(700,155.214,0),(700,310.427,0),(1050,310.427,0),(1050,465.641,0),(1400,465.641,0),(1400,620.855,0),+10 more]
  Start = (13000,-15000,-155.214)
  Subdivisions = 0
FEATURE [Part::FeaturePython] Structure032  label="Stairs"  # Arch/BIM 118 (typed FeaturePython)
  Base = -> Wire020
  FaceMaker = 0
  Height = 3000
  HorizontalArea = 0
  IfcData = IfcUID=0M1L0KRqaHwRzx093rt3ko,+1 more (map truncated)
  IfcType = 118
  Length = 0
  MoveBase = false
  MoveWithHost = true
  Nodes = (2) [(14579.6,-16059.4,-2274.06),(14579.6,-16059.4,725.941)]
  NodesOffset = 0
  Normal = (0,0,0)
  PerimeterLength = 0
  PredefinedType = 0
  VerticalArea = 0
  Width = 200
FEATURE [Part::Part2DObjectPython] Wire021  # Draft 2D object (typed FeaturePython)
  ChamferSize = 0
  Closed = false
  End = (12995,-15005,-100)
  FilletRadius = 0
  Length = 45960
  MakeFace = true
  Placement = pos=(-22005,-14005,-100) rot=(0.707107,0.707107,0;3.14159rad)
  Points = (6) [(0,0,0),(0,-990,0),(-1990,-990,0),(-1990,38000,0),(-1000,38000,0),(-1000,35000,0)]
  Start = (-22005,-14005,-100)
  Subdivisions = 0
FEATURE [Part::Part2DObjectPython] Wire022  # Draft 2D object (typed FeaturePython)
  ChamferSize = 0
  Closed = false
  End = (28005,-10005,-100)
  FilletRadius = 0
  Length = 18990
  MakeFace = true
  Placement = pos=(12995,-11995,-100) rot=(0.707107,0.707107,0;3.14159rad)
  Points = (4) [(0,0,0),(-5,16005,0),(1990,16000,0),(1990,15010,0)]
  Start = (12995,-11995,-100)
  Subdivisions = 0
FEATURE [Part::FeaturePython] Wall012  label="Footing wall003"  # Arch/BIM 150 (typed FeaturePython)
  Align = 0
  Base = -> Wire022
  BlockHeight = 0
  BlockLength = 1000
  CountBroken = 0
  CountEntire = 0
  Face = 0
  Height = 2000
  HorizontalArea = 2.98719e+06
  IfcData = IfcUID=0M1ieCRqaHwRzx093rt3ko,+1 more (map truncated)
  IfcType = 150
  Joint = 0
  Length = 18990
  MakeBlocks = true
  MoveBase = false
  MoveWithHost = true
  Normal = (0,0,-1)
  OffsetFirst = 100
  OffsetSecond = 0
  PerimeterLength = 37659.9
  PredefinedType = 0
  VerticalArea = 7.53198e+07
  Width = 160
FEATURE [Part::FeaturePython] Wall013  label="Footing wall004"  # Arch/BIM 150 (typed FeaturePython)
  Align = 0
  Base = -> Wire021
  BlockHeight = 0
  BlockLength = 1000
  CountBroken = 0
  CountEntire = 0
  Face = 0
  Height = 2000
  HorizontalArea = 7.2512e+06
  IfcData = IfcUID=0M2G9KRqaHwRzx093rt3ko,+1 more (map truncated)
  IfcType = 150
  Joint = 0
  Length = 45960
  MakeBlocks = true
  MoveBase = false
  MoveWithHost = true
  Normal = (0,0,-1)
  OffsetFirst = 0
  OffsetSecond = 0
  PerimeterLength = 90960
  PredefinedType = 0
  VerticalArea = 181920000
  Width = 160
FEATURE [App::DocumentObjectGroup] Group022  label="Footings"
  Group = -> [Wall009,Wall010,Wall011,Structure032,Wall012,Wall013]
FEATURE [App::GeometryPython] BuildingPart  label="Pabellon"  # Arch/BIM 11 (typed FeaturePython)
  Area = 0
  BuildingType = 0
  CompositionType = 0
  ElevationOfRefHeight = 0
  ElevationOfTerrain = 0
  Group = -> [Group022,Group018,Group017,Group013,Group012,Group008,Group007,Group006]
  Height = 0
  IfcData = IfcUID=0L$43IRqaHwRzx093rt3ko,+1 more (map truncated)
  IfcType = 11
  LevelOffset = 0
  LongName = Building
FEATURE [Part::FeaturePython] Site  # Arch/BIM 109 (typed FeaturePython)
  AdditionVolume = 0
  Area = 0
  Compass = false
  CompassRotation = 0
  CompositionType = 0
  Declination = 0
  Elevation = 0
  ExtrusionVector = (0,0,-100000)
  Group = -> [BuildingPart]
  Height = 0
  IfcData = IfcUID=0LzXaeRqaHwRzx093rt3ko,+1 more (map truncated)
  IfcType = 109
  Latitude = 0
  LongName = Site
  Longitude = 0
  OriginOffset = (0,0,0)
  Perimeter = 371158
  ProjectedArea = 0
  RefElevation = 0
  RemoveSplitter = false
  SubtractionVolume = 0
  Terrain = -> Cut
  UpdateDeclination = false
  expr: RefElevation = Elevation.Value
FEATURE [App::FeaturePython] Dimension  # Draft dimension (typed FeaturePython)
  Diameter = false
  Dimline = (55473.6,7010.4,0)
  Direction = (0,0,0)
  Distance = 8320
  End = (56160,6160,0)
  Normal = (0,0,1)
  Start = (47840,6160,0)
FEATURE [App::FeaturePython] Dimension001  # Draft dimension (typed FeaturePython)
  Diameter = false
  Dimline = (64312.8,7010.4,0)
  Direction = (0,0,0)
  Distance = 17170
  End = (73330,6160,0)
  Normal = (0,0,1)
  Start = (56160,6160,0)
FEATURE [App::FeaturePython] Dimension002  # Draft dimension (typed FeaturePython)
  Diameter = false
  Dimline = (72542.4,7010.4,0)
  Direction = (0,0,0)
  Distance = 11470
  End = (84800,-840,0)
  Normal = (0,0,1)
  Start = (73330,-840,0)
FEATURE [App::FeaturePython] Dimension003  # Draft dimension (typed FeaturePython)
  Diameter = false
  Dimline = (89611.2,7010.4,0)
  Direction = (0,0,0)
  Distance = 13360
  End = (98160,160,0)
  Normal = (0,0,1)
  Start = (84800,160,0)
FEATURE [App::FeaturePython] Dimension004  # Draft dimension (typed FeaturePython)
  Diameter = false
  Dimline = (46939.2,4572,0)
  Direction = (0,0,0)
  Distance = 21320
  End = (47840,6160,0)
  Normal = (0,0,1)
  Start = (47840,-15160,0)
FEATURE [App::FeaturePython] Dimension005  # Draft dimension (typed FeaturePython)
  Diameter = false
  Dimline = (-3500,-10500,0)
  Direction = (0,0,0)
  Distance = 9000
  End = (-7007.5,-15000,0)
  Normal = (0,0,1)
  Start = (-7007.5,-6000,0)
FEATURE [App::FeaturePython] Dimension006  # Draft dimension (typed FeaturePython)
  Diameter = false
  Dimline = (-7300,-13600,0)
  Direction = (0,0,0)
  Distance = 20000
  End = (-2000,-14660,0)
  Normal = (0,0,1)
  Start = (-22000,-14660,0)
FEATURE [App::FeaturePython] Text  # WARN: FeaturePython — macro-defined, semantics opaque (R4)
  Placement = pos=(-13800,-10300,0) rot=(0,0,1;0rad)
  Text = SWIMMING POOL
FEATURE [App::DocumentObjectGroup] Group024  label="plan annotations (for TechDraw views)"
  Group = -> [Dimension005,Text,Dimension006]
FEATURE [App::FeaturePython] Section  # WARN: FeaturePython — macro-defined, semantics opaque (R4)
  Clip = false
  Objects = -> [BuildingPart,Group024]
  OnlySolids = true
  Placement = pos=(3002.5,-4647.5,1600) rot=(0,0,1;0rad)
  UseMaterialColorForFill = false
FEATURE [Part::Part2DObjectPython] Shape2DView  # Draft 2D object (typed FeaturePython)
  Base = -> Section
  FuseArch = true
  HiddenLines = false
  InPlace = true
  Placement = pos=(70000,0,0) rot=(0,0,1;0rad)
  Projection = (-0.189627,-0.656588,0.730023)
  ProjectionMode = 0
  SegmentLength = 0.05
  Tessellation = false
  VisibleOnly = false
FEATURE [Part::Part2DObjectPython] Shape2DView001  # Draft 2D object (typed FeaturePython)
  Base = -> Section
  FuseArch = true
  HiddenLines = false
  InPlace = false
  Placement = pos=(70000,0,0) rot=(0,0,1;0rad)
  Projection = (-0.189627,-0.656588,0.730023)
  ProjectionMode = 3
  SegmentLength = 0.05
  Tessellation = false
  VisibleOnly = false
FEATURE [App::DocumentObjectGroup] Group023  label="2D plan output"
  Group = -> [Shape2DView,Shape2DView001,Dimension,Dimension001,Dimension002,Dimension003,Dimension004]
FEATURE [TechDraw::DrawSVGTemplate] Template
  EditableTexts = Designed_by_Name=Yorik; FC-Date=04.06.2019; FC-SC=1:200; FC-Title=Barcelona Pavillion; Subtitle=Ground floor
  Height = 210
  Orientation = 1
  Width = 297
FEATURE [TechDraw::DrawViewArch] ArchView
  AllOn = false
  FillSpaces = false
  FontSize = 6
  LineWidth = 0.15
  LockPosition = false
  RenderMode = 0
  Rotation = 0
  Scale = 0.005
  ScaleType = 2
  ShowFill = false
  ShowHidden = false
  Source = -> Section
  Symbol = <blob: 238588 chars omitted>
  X = 148.5
  Y = 134
FEATURE [TechDraw::DrawPage] Page  label="Page 01 - TechDraw + Arch view"
  KeepUpdated = true
  NextBalloonIndex = 1
  ProjectionType = 0
  Template = -> Template
  Views = -> [ArchView]
FEATURE [TechDraw::DrawSVGTemplate] Template001
  EditableTexts = Designed_by_Name=Designed by Name; Drawing_number=Drawing number; FC-Date=Date; FC-SC=Scale; FC-SH=Sheet; FC-Title=Title; Subtitle=Subtitle; Weight=Weight
  Height = 210
  Orientation = 1
  Width = 297
FEATURE [TechDraw::DrawViewPart] View
  CoarseView = false
  Direction = (0,0,1)
  Focus = 100
  HardHidden = false
  IsoCount = 0
  IsoHidden = false
  IsoVisible = false
  LockPosition = false
  Perspective = false
  Rotation = 0
  Scale = 0.005
  ScaleType = 2
  SeamHidden = false
  SeamVisible = false
  SmoothHidden = false
  SmoothVisible = false
  Source = -> [BuildingPart]
  X = 148.032
  Y = 130.987
FEATURE [TechDraw::DrawViewDimension] Dimension007
  Arbitrary = false
  FormatSpec = %.3f
  LockPosition = false
  MeasureType = 1
  OverTolerance = 0
  References2D = -> [View]
  Rotation = 0
  ScaleType = 0
  Type = 2
  UnderTolerance = 0
  X = -35.6733
  Y = -30.128
FEATURE [TechDraw::DrawViewDimension] Dimension008
  Arbitrary = false
  FormatSpec = %.3f
  LockPosition = false
  MeasureType = 1
  OverTolerance = 0
  References2D = -> [View]
  Rotation = 0
  ScaleType = 0
  Type = 1
  UnderTolerance = 0
  X = -74.8219
  Y = -40.3518
FEATURE [TechDraw::DrawPage] Page001  label="Page 02 - Pure TechDraw"
  KeepUpdated = true
  NextBalloonIndex = 1
  ProjectionType = 0
  Template = -> Template001
  Views = -> [View,Dimension007,Dimension008]
FEATURE [Spreadsheet::Sheet] Result
  cells = A1=Description; B1=Value; C1=Unit; A2=Exterior walls area; B2=643.0919987999988; C2=m²; A3=Interior walls area; B3=54.78000000000134; C3=m²; A4=Windows area; B4=165.39993; C4=m²; A5=Roof slab area; B5=381.9599999999993; C5=m²
FEATURE [App::FeaturePython] Schedule  # WARN: FeaturePython — macro-defined, semantics opaque (R4)
  Description = Exterior walls area | Interior walls area | Windows area | Roof slab area
  Filter = type:Wall | type:Wall | type:Window
  Objects = Group014 | Group015 | Group006
  Result = -> Result
  Unit = m² | m² | m² | m²
  Value = object.VerticalArea | object.VerticalArea | object.Area | object.HorizontalArea
FEATURE [Spreadsheet::Sheet] Result001
  cells = A1=Vertical walls area; A2==Label; B2=VerticalArea; A3=Wall; B3==246192000(mm ^ 2); A4=Wall001; B4==113940000(mm ^ 2); A5=Wall002; B5==206079999.6(mm ^ 2); A6=Wall003; B6==44959999.2(mm ^ 2); A7=Wall004; B7==31920000(mm ^ 2); A8=Wall005; B8==27780000(mm ^ 2); A9=Wall006; B9==21360000(mm ^ 2); A10=Wall007; B10==5640000(mm ^ 2); A11=Footing wall; B11==155960000(mm ^ 2); A12=Footing wall001; B12==140637000.55(mm ^ 2); A13=Footing wall002; B13==60165000(mm ^ 2); A14=Footing wall003; B14==75319823.7(mm ^ 2); A15=Footing wall004; B15==181920000(mm ^ 2); A18=Total vertical walls area; A19=Sum(VerticalArea); A20==1311873823.05(mm ^ 2); A23=Windows area; A24==Label; B24=Area; A25=Window; B25==0(mm ^ 2); A26=Window 200x300; B26==6000000(mm ^ 2); A27=Window 195x300; B27==5850000(mm ^ 2); A28=Window 197x300; B28==5925000(mm ^ 2); A29=Window 102x300; B29==3075000(mm ^ 2); A30=Window top 95x90; B30==855000(mm ^ 2); A31=Window 100x300 009; B31==3000000(mm ^ 2); A32=Window 100x300 008; B32==3000000(mm ^ 2); A33=Window 100x300 007; B33==3000000(mm ^ 2); A34=Window 100x300 006; B34==3000000(mm ^ 2); A35=Window 100x300 005; B35==3000000(mm ^ 2); A36=Window 100x300 004; B36==3000000(mm ^ 2); A37=Window 100x300 003; B37==3000000(mm ^ 2); A38=Window 100x300 002; B38==3000000(mm ^ 2); A39=Window 100x300 001; B39==3000000(mm ^ 2); A40=Window 100x300 ; B40==3000000(mm ^ 2); A41=Window 304x300 001; B41==9120000(mm ^ 2); A42=Window 309x300 001; B42==9270000(mm ^ 2); A43=Window 309x300 ; B43==9270000(mm ^ 2); A44=Window 304x300 ; B44==9120000(mm ^ 2); A45=Window 338x300 002; B45==11333310(mm ^ 2); A46=Window 338x300 001; B46==11333310(mm ^ 2); A47=Window 338x300 ; B47==11333310(mm ^ 2); A48=Window 33x300 001; B48==990000(mm ^ 2); A49=Window top 200x90 ; B49==1800000(mm ^ 2); A50=Window top 200x90 001; B50==1800000(mm ^ 2); A51=Window 33x300 ; B51==990000(mm ^ 2); A52=Window 89x300 007; B52==2685000(mm ^ 2); A53=Window 89x300 006; B53==2685000(mm ^ 2); A54=Window 89x300 005; B54==2685000(mm ^ 2); A55=Window 89x300 004; B55==2685000(mm ^ 2); A56=Window 89x300 003; B56==2685000(mm ^ 2); A57=Window 89x300 002; B57==2685000(mm ^ 2); A58=Window 89x300 001; B58==2685000(mm ^ 2); A59=Window 89x300 ; B59==2685000(mm ^ 2); A62=Total window area; A63=Sum(Area); A64==149544930(mm ^ 2)
FEATURE [App::FeaturePython] Report  # WARN: FeaturePython — macro-defined, semantics opaque (R4)
  Result = -> Result001
  SkipComputing = false
